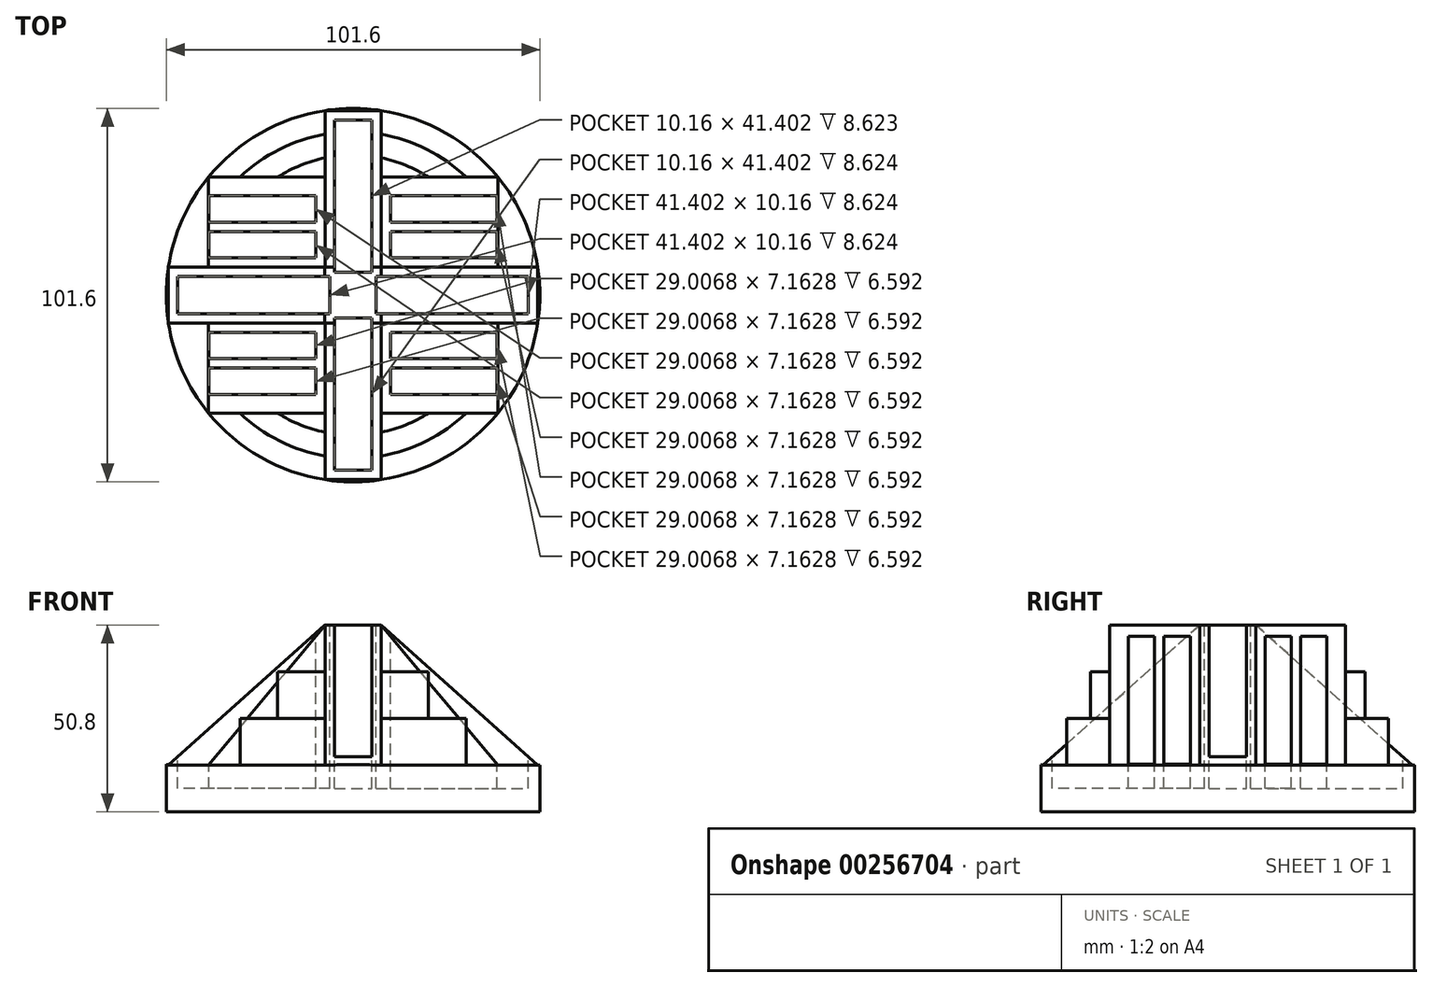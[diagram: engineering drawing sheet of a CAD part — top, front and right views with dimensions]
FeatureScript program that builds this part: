
annotation { "Feature Type Name" : "Feature", "Feature Type Description" : "" }
export const myFeature = defineFeature(function(context is Context, id is Id, definition is map)
    precondition{}
    {
        {
            var Q0;
            Q0=qCreatedBy(makeId("Top.planeOp"),FACE);
            cPlane(context, id + "F0", {"entities" : qUnion([Q0]), "cplaneType" : CPlaneType.OFFSET, "offset" : 50.8 * mm, "width" : 152.4 * mm, "height" : 152.4 * mm});
        }
        {
            var Q0;
            Q0=qCreatedBy(makeId("Top.planeOp"),FACE);
            var sketch = newSketch(context, id + "F1", { "sketchPlane" : qUnion([Q0])});
            skCircle(sketch, "E0", {"center": v(0, 0) * mm, "radius": 50.8 * mm});
            skArc(sketch, "E1", {"start": v(7.62, -43.8) * mm, "mid": v(44.45, 0) * mm, "end": v(7.62, 43.8) * mm});
            skArc(sketch, "E2", {"start": v(7.62, -37.33) * mm, "mid": v(38.1, 0) * mm, "end": v(7.62, 37.33) * mm});
            skCircle(sketch, "E3", {"center": v(0, 0) * mm, "radius": 25.4 * mm});
            skLineSegment(sketch, "E4", {"start": v(-7.62, -24.23) * mm, "end": v(-7.62, -50.23) * mm});
            skLineSegment(sketch, "E5", {"start": v(7.62, -24.23) * mm, "end": v(7.62, -50.23) * mm});
            skLineSegment(sketch, "E6", {"start": v(-7.62, 24.23) * mm, "end": v(-7.62, 50.23) * mm});
            skLineSegment(sketch, "E7", {"start": v(7.62, 24.23) * mm, "end": v(7.62, 50.23) * mm});
            skPoint(sketch, "E8.orphan", {"position": v(0, -25.4) * mm});
            skPoint(sketch, "E9.end.orphan", {"position": v(-3.8, -50.66) * mm});
            skArc(sketch, "E10.trimOffspring", {"start": v(-7.62, 37.33) * mm, "mid": v(-38.1, 0) * mm, "end": v(-7.62, -37.33) * mm});
            skArc(sketch, "E11.trimOffspring", {"start": v(-7.62, 43.8) * mm, "mid": v(-44.45, 0) * mm, "end": v(-7.62, -43.8) * mm});
            skArc(sketch, "E12", {"start": v(-7.62, -43.8) * mm, "mid": v(0, -44.45) * mm, "end": v(7.62, -43.8) * mm});
            skArc(sketch, "E13", {"start": v(-7.62, -37.33) * mm, "mid": v(0, -38.1) * mm, "end": v(7.62, -37.33) * mm});
            skCircle(sketch, "E14", {"center": v(0, 0) * mm, "radius": 31.75 * mm});
            skArc(sketch, "E15.trimOffspring", {"start": v(7.62, 43.8) * mm, "mid": v(0, 44.45) * mm, "end": v(-7.62, 43.8) * mm});
            skArc(sketch, "E16.trimOffspring", {"start": v(7.62, 37.33) * mm, "mid": v(0, 38.1) * mm, "end": v(-7.62, 37.33) * mm});
            skLineSegment(sketch, "E17", {"start": v(-7.62, -24.23) * mm, "end": v(-7.62, 24.23) * mm});
            skLineSegment(sketch, "E18", {"start": v(7.62, 24.23) * mm, "end": v(7.62, -24.23) * mm});
            skLineSegment(sketch, "E19", {"start": v(0, 7.62) * mm, "end": v(-50.23, 7.62) * mm});
            skLineSegment(sketch, "E20", {"start": v(0, 7.62) * mm, "end": v(50.23, 7.62) * mm});
            skLineSegment(sketch, "E21", {"start": v(0, -7.62) * mm, "end": v(50.23, -7.62) * mm});
            skLineSegment(sketch, "E22", {"start": v(0, -7.62) * mm, "end": v(-50.23, -7.62) * mm});
            skLineSegment(sketch, "E23", {"start": v(-17.78, 7.62) * mm, "end": v(7.62, -17.78) * mm});
            skLineSegment(sketch, "E24", {"start": v(-7.62, 17.78) * mm, "end": v(17.78, -7.62) * mm});
            skLineSegment(sketch, "E25", {"start": v(7.62, 17.78) * mm, "end": v(-17.78, -7.62) * mm});
            skLineSegment(sketch, "E26", {"start": v(17.78, 7.62) * mm, "end": v(-7.62, -17.78) * mm});
            skLineSegment(sketch, "E27", {"start": v(-7.62, -19.86) * mm, "end": v(-20.32, -19.86) * mm});
            skLineSegment(sketch, "E28", {"start": v(-20.32, -19.86) * mm, "end": v(-46.76, -19.86) * mm});
            skLineSegment(sketch, "E29.trimOffspring", {"start": v(-20.32, -32.1) * mm, "end": v(-20.32, -32.23) * mm});
            skPoint(sketch, "E30.start.orphan", {"position": v(-20.32, -7.62) * mm});
            skLineSegment(sketch, "E31", {"start": v(-7.62, -32.1) * mm, "end": v(-39.37, -32.1) * mm});
            skLineSegment(sketch, "E32", {"start": v(-7.62, 19.86) * mm, "end": v(-46.76, 19.86) * mm});
            skLineSegment(sketch, "E33", {"start": v(-7.62, 32.1) * mm, "end": v(-39.37, 32.1) * mm});
            skLineSegment(sketch, "E34", {"start": v(7.62, 32.1) * mm, "end": v(39.37, 32.1) * mm});
            skLineSegment(sketch, "E35", {"start": v(7.62, 19.86) * mm, "end": v(46.76, 19.86) * mm});
            skLineSegment(sketch, "E36", {"start": v(7.62, -19.86) * mm, "end": v(46.76, -19.86) * mm});
            skLineSegment(sketch, "E37", {"start": v(7.62, -32.1) * mm, "end": v(39.37, -32.1) * mm});
            skSolve(sketch);
        }
        {
            var Q0;
            {var subQ5=sQuery(id+"F1.wireOp",EDGE,"E11.trimOffspring");Q0=makeQuery(id+"F1.imprint","IMPRINT",FACE,{"disambiguationData":[TD([[makeQuery(id+"F1.imprint","IMPRINT",EDGE,{"derivedFrom":subQ5}),-1.0]])]});}
            var Q1;
            {var subQ5=sQuery(id+"F1.wireOp",EDGE,"E15.trimOffspring");Q1=makeQuery(id+"F1.imprint","IMPRINT",FACE,{"disambiguationData":[TD([[makeQuery(id+"F1.imprint","IMPRINT",EDGE,{"derivedFrom":subQ5}),-1.0]])]});}
            var Q2;
            {var subQ5=sQuery(id+"F1.wireOp",EDGE,"E1");Q2=makeQuery(id+"F1.imprint","IMPRINT",FACE,{"disambiguationData":[TD([[makeQuery(id+"F1.imprint","IMPRINT",EDGE,{"derivedFrom":subQ5}),-1.0]])]});}
            var Q3;
            {var subQ5=sQuery(id+"F1.wireOp",EDGE,"E12");Q3=makeQuery(id+"F1.imprint","IMPRINT",FACE,{"disambiguationData":[TD([[makeQuery(id+"F1.imprint","IMPRINT",EDGE,{"derivedFrom":subQ5}),-1.0]])]});}
            extrude(context, id + "F2", {"entities" : qUnion([Q0, Q1, Q2, Q3]), "depth" : 12.7 * mm});
        }
        {
            var Q0;
            {var subQ0=sQuery(id+"F1.wireOp",EDGE,"E10.trimOffspring");Q0=makeQuery(id+"F1.imprint","IMPRINT",FACE,{"disambiguationData":[TD([[makeQuery(id+"F1.imprint","IMPRINT",EDGE,{"derivedFrom":subQ0}),-1.0]])]});}
            var Q1;
            {var subQ0=sQuery(id+"F1.wireOp",EDGE,"E1");Q1=makeQuery(id+"F1.imprint","IMPRINT",FACE,{"disambiguationData":[TD([[makeQuery(id+"F1.imprint","IMPRINT",EDGE,{"derivedFrom":subQ0}),1.0]])]});}
            var Q2;
            {var subQ2=sQuery(id+"F1.wireOp",EDGE,"E15.trimOffspring");Q2=makeQuery(id+"F1.imprint","IMPRINT",FACE,{"disambiguationData":[TD([[makeQuery(id+"F1.imprint","IMPRINT",EDGE,{"derivedFrom":subQ2}),1.0]])]});}
            var Q3;
            {var subQ2=sQuery(id+"F1.wireOp",EDGE,"E12");Q3=makeQuery(id+"F1.imprint","IMPRINT",FACE,{"disambiguationData":[TD([[makeQuery(id+"F1.imprint","IMPRINT",EDGE,{"derivedFrom":subQ2}),1.0]])]});}
            var Q4;
            {var subQ0=sQuery(id+"F1.wireOp",EDGE,"E10.trimOffspring");var subQ5=sQuery(id+"F1.wireOp",EDGE,"KU0cdiGB-8eOj-Trs3-v5YD-3LzdnCRRimhK");var subQ6=makeQuery(id+"F1.imprint","INTERSECT",VERTEX,{"derivedFrom":[subQ0,subQ5]});Q4=makeQuery(id+"F1.imprint","IMPRINT",FACE,{"disambiguationData":[TD([[makeQuery(id+"F1.imprint","IMPRINT",EDGE,{"disambiguationData":[TD([[subQ6,-1.0]])],"derivedFrom":subQ5}),-1.0]])]});}
            var Q5;
            {var subQ0=sQuery(id+"F1.wireOp",EDGE,"KU0cdiGB-8eOj-Trs3-v5YD-3LzdnCRRimhK");var subQ1=sQuery(id+"F1.wireOp",EDGE,"E10.trimOffspring");var subQ2=makeQuery(id+"F1.imprint","INTERSECT",VERTEX,{"derivedFrom":[subQ1,subQ0]});Q5=makeQuery(id+"F1.imprint","IMPRINT",FACE,{"disambiguationData":[TD([[makeQuery(id+"F1.imprint","IMPRINT",EDGE,{"disambiguationData":[TD([[subQ2,-1.0]])],"derivedFrom":subQ1}),-1.0]])]});}
            var Q6;
            {var subQ0=sQuery(id+"F1.wireOp",EDGE,"n5LII22h-w08l-qE72-yfr9-18N67uZxNTdQ");var subQ1=sQuery(id+"F1.wireOp",EDGE,"E10.trimOffspring");var subQ2=makeQuery(id+"F1.imprint","INTERSECT",VERTEX,{"derivedFrom":[subQ1,subQ0]});Q6=makeQuery(id+"F1.imprint","IMPRINT",FACE,{"disambiguationData":[TD([[makeQuery(id+"F1.imprint","IMPRINT",EDGE,{"disambiguationData":[TD([[subQ2,-1.0]])],"derivedFrom":subQ1}),-1.0]])]});}
            var Q7;
            {var subQ0=sQuery(id+"F1.wireOp",EDGE,"E19");var subQ1=sQuery(id+"F1.wireOp",EDGE,"E10.trimOffspring");var subQ2=makeQuery(id+"F1.imprint","INTERSECT",VERTEX,{"derivedFrom":[subQ1,subQ0]});Q7=makeQuery(id+"F1.imprint","IMPRINT",FACE,{"disambiguationData":[TD([[makeQuery(id+"F1.imprint","IMPRINT",EDGE,{"disambiguationData":[TD([[subQ2,-1.0]])],"derivedFrom":subQ1}),-1.0]])]});}
            var Q8;
            {var subQ0=sQuery(id+"F1.wireOp",EDGE,"E22");var subQ1=sQuery(id+"F1.wireOp",EDGE,"E10.trimOffspring");var subQ2=makeQuery(id+"F1.imprint","INTERSECT",VERTEX,{"derivedFrom":[subQ1,subQ0]});Q8=makeQuery(id+"F1.imprint","IMPRINT",FACE,{"disambiguationData":[TD([[makeQuery(id+"F1.imprint","IMPRINT",EDGE,{"disambiguationData":[TD([[subQ2,-1.0]])],"derivedFrom":subQ1}),-1.0]])]});}
            var Q9;
            {var subQ0=sQuery(id+"F1.wireOp",EDGE,"E28");var subQ1=sQuery(id+"F1.wireOp",EDGE,"E10.trimOffspring");var subQ2=makeQuery(id+"F1.imprint","INTERSECT",VERTEX,{"derivedFrom":[subQ1,subQ0]});Q9=makeQuery(id+"F1.imprint","IMPRINT",FACE,{"disambiguationData":[TD([[makeQuery(id+"F1.imprint","IMPRINT",EDGE,{"disambiguationData":[TD([[subQ2,-1.0]])],"derivedFrom":subQ1}),-1.0]])]});}
            var Q10;
            {var subQ1=sQuery(id+"F1.wireOp",EDGE,"E10.trimOffspring");var subQ5=sQuery(id+"F1.wireOp",EDGE,"E25");var subQ6=makeQuery(id+"F1.imprint","INTERSECT",VERTEX,{"derivedFrom":[subQ1,subQ5]});Q10=makeQuery(id+"F1.imprint","IMPRINT",FACE,{"disambiguationData":[TD([[makeQuery(id+"F1.imprint","IMPRINT",EDGE,{"disambiguationData":[TD([[subQ6,-1.0]])],"derivedFrom":subQ1}),-1.0]])]});}
            var Q11;
            {var subQ0=sQuery(id+"F1.wireOp",EDGE,"E31");var subQ1=sQuery(id+"F1.wireOp",EDGE,"E11.trimOffspring");var subQ2=makeQuery(id+"F1.imprint","INTERSECT",VERTEX,{"derivedFrom":[subQ1,subQ0]});Q11=makeQuery(id+"F1.imprint","IMPRINT",FACE,{"disambiguationData":[TD([[makeQuery(id+"F1.imprint","IMPRINT",EDGE,{"disambiguationData":[TD([[subQ2,-1.0]])],"derivedFrom":subQ1}),1.0]])]});}
            var Q12;
            {var subQ0=sQuery(id+"F1.wireOp",EDGE,"E26");var subQ1=sQuery(id+"F1.wireOp",EDGE,"E10.trimOffspring");var subQ2=makeQuery(id+"F1.imprint","INTERSECT",VERTEX,{"derivedFrom":[subQ1,subQ0]});Q12=makeQuery(id+"F1.imprint","IMPRINT",FACE,{"disambiguationData":[TD([[makeQuery(id+"F1.imprint","IMPRINT",EDGE,{"disambiguationData":[TD([[subQ2,-1.0]])],"derivedFrom":subQ1}),-1.0]])]});}
            var Q13;
            {var subQ0=sQuery(id+"F1.wireOp",EDGE,"E32");var subQ1=sQuery(id+"F1.wireOp",EDGE,"E10.trimOffspring");var subQ2=makeQuery(id+"F1.imprint","INTERSECT",VERTEX,{"derivedFrom":[subQ1,subQ0]});Q13=makeQuery(id+"F1.imprint","IMPRINT",FACE,{"disambiguationData":[TD([[makeQuery(id+"F1.imprint","IMPRINT",EDGE,{"disambiguationData":[TD([[subQ2,-1.0]])],"derivedFrom":subQ1}),-1.0]])]});}
            var Q14;
            {var subQ0=sQuery(id+"F1.wireOp",EDGE,"E33");var subQ1=sQuery(id+"F1.wireOp",EDGE,"E10.trimOffspring");var subQ2=makeQuery(id+"F1.imprint","INTERSECT",VERTEX,{"derivedFrom":[subQ1,subQ0]});Q14=makeQuery(id+"F1.imprint","IMPRINT",FACE,{"disambiguationData":[TD([[makeQuery(id+"F1.imprint","IMPRINT",EDGE,{"disambiguationData":[TD([[subQ2,-1.0]])],"derivedFrom":subQ1}),-1.0]])]});}
            var Q15;
            {var subQ0=sQuery(id+"F1.wireOp",EDGE,"E10.trimOffspring");var subQ5=sQuery(id+"F1.wireOp",EDGE,"E33");var subQ7=makeQuery(id+"F1.imprint","INTERSECT",VERTEX,{"derivedFrom":[subQ0,subQ5]});Q15=makeQuery(id+"F1.imprint","IMPRINT",FACE,{"disambiguationData":[TD([[makeQuery(id+"F1.imprint","IMPRINT",EDGE,{"disambiguationData":[TD([[subQ7,-1.0]])],"derivedFrom":subQ5}),-1.0]])]});}
            extrude(context, id + "F3", {"entities" : qUnion([Q0, Q1, Q2, Q3, Q4, Q5, Q6, Q7, Q8, Q9, Q10, Q11, Q12, Q13, Q14, Q15]), "operationType" : NewBodyOperationType.ADD, "depth" : 25.4 * mm});
        }
        {
            var Q0;
            {var subQ0=sQuery(id+"F1.wireOp",EDGE,"E13");Q0=makeQuery(id+"F1.imprint","IMPRINT",FACE,{"disambiguationData":[TD([[makeQuery(id+"F1.imprint","IMPRINT",EDGE,{"derivedFrom":subQ0}),1.0]])]});}
            var Q1;
            {var subQ0=sQuery(id+"F1.wireOp",EDGE,"E10.trimOffspring");Q1=makeQuery(id+"F1.imprint","IMPRINT",FACE,{"disambiguationData":[TD([[makeQuery(id+"F1.imprint","IMPRINT",EDGE,{"derivedFrom":subQ0}),1.0]])]});}
            var Q2;
            {var subQ0=sQuery(id+"F1.wireOp",EDGE,"E2");Q2=makeQuery(id+"F1.imprint","IMPRINT",FACE,{"disambiguationData":[TD([[makeQuery(id+"F1.imprint","IMPRINT",EDGE,{"derivedFrom":subQ0}),1.0]])]});}
            var Q3;
            {var subQ0=sQuery(id+"F1.wireOp",EDGE,"E16.trimOffspring");Q3=makeQuery(id+"F1.imprint","IMPRINT",FACE,{"disambiguationData":[TD([[makeQuery(id+"F1.imprint","IMPRINT",EDGE,{"derivedFrom":subQ0}),1.0]])]});}
            var Q4;
            {var subQ0=sQuery(id+"F1.wireOp",EDGE,"n5LII22h-w08l-qE72-yfr9-18N67uZxNTdQ");var subQ1=sQuery(id+"F1.wireOp",EDGE,"E10.trimOffspring");var subQ2=makeQuery(id+"F1.imprint","INTERSECT",VERTEX,{"derivedFrom":[subQ1,subQ0]});Q4=makeQuery(id+"F1.imprint","IMPRINT",FACE,{"disambiguationData":[TD([[makeQuery(id+"F1.imprint","IMPRINT",EDGE,{"disambiguationData":[TD([[subQ2,-1.0]])],"derivedFrom":subQ1}),1.0]])]});}
            var Q5;
            {var subQ0=sQuery(id+"F1.wireOp",EDGE,"KU0cdiGB-8eOj-Trs3-v5YD-3LzdnCRRimhK");var subQ1=sQuery(id+"F1.wireOp",EDGE,"E10.trimOffspring");var subQ2=makeQuery(id+"F1.imprint","INTERSECT",VERTEX,{"derivedFrom":[subQ1,subQ0]});Q5=makeQuery(id+"F1.imprint","IMPRINT",FACE,{"disambiguationData":[TD([[makeQuery(id+"F1.imprint","IMPRINT",EDGE,{"disambiguationData":[TD([[subQ2,-1.0]])],"derivedFrom":subQ1}),1.0]])]});}
            var Q6;
            {var subQ1=sQuery(id+"F1.wireOp",EDGE,"E6");var subQ3=sQuery(id+"F1.wireOp",EDGE,"E14");var subQ4=makeQuery(id+"F1.imprint","INTERSECT",VERTEX,{"derivedFrom":[subQ1,subQ3]});Q6=makeQuery(id+"F1.imprint","IMPRINT",FACE,{"disambiguationData":[TD([[makeQuery(id+"F1.imprint","IMPRINT",EDGE,{"disambiguationData":[TD([[subQ4,-1.0]])],"derivedFrom":subQ3}),-1.0]])]});}
            var Q7;
            {var subQ0=sQuery(id+"F1.wireOp",EDGE,"E7");var subQ5=sQuery(id+"F1.wireOp",EDGE,"E14");var subQ6=makeQuery(id+"F1.imprint","INTERSECT",VERTEX,{"derivedFrom":[subQ0,subQ5]});Q7=makeQuery(id+"F1.imprint","IMPRINT",FACE,{"disambiguationData":[TD([[makeQuery(id+"F1.imprint","IMPRINT",EDGE,{"disambiguationData":[TD([[subQ6,1.0]])],"derivedFrom":subQ5}),-1.0]])]});}
            var Q8;
            {var subQ0=sQuery(id+"F1.wireOp",EDGE,"E19");var subQ1=sQuery(id+"F1.wireOp",EDGE,"E10.trimOffspring");var subQ2=makeQuery(id+"F1.imprint","INTERSECT",VERTEX,{"derivedFrom":[subQ1,subQ0]});Q8=makeQuery(id+"F1.imprint","IMPRINT",FACE,{"disambiguationData":[TD([[makeQuery(id+"F1.imprint","IMPRINT",EDGE,{"disambiguationData":[TD([[subQ2,-1.0]])],"derivedFrom":subQ1}),1.0]])]});}
            var Q9;
            {var subQ0=sQuery(id+"F1.wireOp",EDGE,"E22");var subQ1=sQuery(id+"F1.wireOp",EDGE,"E10.trimOffspring");var subQ2=makeQuery(id+"F1.imprint","INTERSECT",VERTEX,{"derivedFrom":[subQ1,subQ0]});Q9=makeQuery(id+"F1.imprint","IMPRINT",FACE,{"disambiguationData":[TD([[makeQuery(id+"F1.imprint","IMPRINT",EDGE,{"disambiguationData":[TD([[subQ2,-1.0]])],"derivedFrom":subQ1}),1.0]])]});}
            var Q10;
            {var subQ0=sQuery(id+"F1.wireOp",EDGE,"E25");var subQ1=sQuery(id+"F1.wireOp",EDGE,"E10.trimOffspring");var subQ2=makeQuery(id+"F1.imprint","INTERSECT",VERTEX,{"derivedFrom":[subQ1,subQ0]});Q10=makeQuery(id+"F1.imprint","IMPRINT",FACE,{"disambiguationData":[TD([[makeQuery(id+"F1.imprint","IMPRINT",EDGE,{"disambiguationData":[TD([[subQ2,-1.0]])],"derivedFrom":subQ1}),1.0]])]});}
            var Q11;
            {var subQ3=sQuery(id+"F1.wireOp",EDGE,"E14");var subQ7=sQuery(id+"F1.wireOp",EDGE,"E4");var subQ8=makeQuery(id+"F1.imprint","INTERSECT",VERTEX,{"derivedFrom":[subQ7,subQ3]});Q11=makeQuery(id+"F1.imprint","IMPRINT",FACE,{"disambiguationData":[TD([[makeQuery(id+"F1.imprint","IMPRINT",EDGE,{"disambiguationData":[TD([[subQ8,-1.0]])],"derivedFrom":subQ7}),-1.0]])]});}
            var Q12;
            {var subQ1=sQuery(id+"F1.wireOp",EDGE,"E2");var subQ5=sQuery(id+"F1.wireOp",EDGE,"dChad7VG-r3lr-Y0ra-zuCQ-UW0r8UzcO7aT");var subQ6=makeQuery(id+"F1.imprint","INTERSECT",VERTEX,{"derivedFrom":[subQ1,subQ5]});Q12=makeQuery(id+"F1.imprint","IMPRINT",FACE,{"disambiguationData":[TD([[makeQuery(id+"F1.imprint","IMPRINT",EDGE,{"disambiguationData":[TD([[subQ6,-1.0]])],"derivedFrom":subQ1}),1.0]])]});}
            var Q13;
            {var subQ0=sQuery(id+"F1.wireOp",EDGE,"E23");var subQ1=sQuery(id+"F1.wireOp",EDGE,"E2");var subQ2=makeQuery(id+"F1.imprint","INTERSECT",VERTEX,{"derivedFrom":[subQ1,subQ0]});Q13=makeQuery(id+"F1.imprint","IMPRINT",FACE,{"disambiguationData":[TD([[makeQuery(id+"F1.imprint","IMPRINT",EDGE,{"disambiguationData":[TD([[subQ2,-1.0]])],"derivedFrom":subQ1}),1.0]])]});}
            var Q14;
            {var subQ0=sQuery(id+"F1.wireOp",EDGE,"E24");var subQ1=sQuery(id+"F1.wireOp",EDGE,"E2");var subQ2=makeQuery(id+"F1.imprint","INTERSECT",VERTEX,{"derivedFrom":[subQ1,subQ0]});Q14=makeQuery(id+"F1.imprint","IMPRINT",FACE,{"disambiguationData":[TD([[makeQuery(id+"F1.imprint","IMPRINT",EDGE,{"disambiguationData":[TD([[subQ2,-1.0]])],"derivedFrom":subQ1}),1.0]])]});}
            var Q15;
            {var subQ0=sQuery(id+"F1.wireOp",EDGE,"E21");var subQ1=sQuery(id+"F1.wireOp",EDGE,"E2");var subQ2=makeQuery(id+"F1.imprint","INTERSECT",VERTEX,{"derivedFrom":[subQ1,subQ0]});Q15=makeQuery(id+"F1.imprint","IMPRINT",FACE,{"disambiguationData":[TD([[makeQuery(id+"F1.imprint","IMPRINT",EDGE,{"disambiguationData":[TD([[subQ2,-1.0]])],"derivedFrom":subQ1}),1.0]])]});}
            var Q16;
            {var subQ0=sQuery(id+"F1.wireOp",EDGE,"E20");var subQ1=sQuery(id+"F1.wireOp",EDGE,"E2");var subQ2=makeQuery(id+"F1.imprint","INTERSECT",VERTEX,{"derivedFrom":[subQ1,subQ0]});Q16=makeQuery(id+"F1.imprint","IMPRINT",FACE,{"disambiguationData":[TD([[makeQuery(id+"F1.imprint","IMPRINT",EDGE,{"disambiguationData":[TD([[subQ2,-1.0]])],"derivedFrom":subQ1}),1.0]])]});}
            var Q17;
            {var subQ0=sQuery(id+"F1.wireOp",EDGE,"SVIod6WE-LFFt-Ms97-owyS-8ShU65W6W8it");var subQ1=sQuery(id+"F1.wireOp",EDGE,"E2");var subQ2=makeQuery(id+"F1.imprint","INTERSECT",VERTEX,{"derivedFrom":[subQ1,subQ0]});Q17=makeQuery(id+"F1.imprint","IMPRINT",FACE,{"disambiguationData":[TD([[makeQuery(id+"F1.imprint","IMPRINT",EDGE,{"disambiguationData":[TD([[subQ2,-1.0]])],"derivedFrom":subQ1}),1.0]])]});}
            var Q18;
            {var subQ0=sQuery(id+"F1.wireOp",EDGE,"E25");var subQ1=sQuery(id+"F1.wireOp",EDGE,"E14");var subQ2=makeQuery(id+"F1.imprint","INTERSECT",VERTEX,{"derivedFrom":[subQ1,subQ0]});Q18=makeQuery(id+"F1.imprint","IMPRINT",FACE,{"disambiguationData":[TD([[makeQuery(id+"F1.imprint","IMPRINT",EDGE,{"disambiguationData":[TD([[subQ2,-1.0]])],"derivedFrom":subQ1}),-1.0]])]});}
            var Q19;
            {var subQ0=sQuery(id+"F1.wireOp",EDGE,"E30");var subQ1=sQuery(id+"F1.wireOp",EDGE,"E14");var subQ2=makeQuery(id+"F1.imprint","INTERSECT",VERTEX,{"derivedFrom":[subQ1,subQ0]});Q19=makeQuery(id+"F1.imprint","IMPRINT",FACE,{"disambiguationData":[TD([[makeQuery(id+"F1.imprint","IMPRINT",EDGE,{"disambiguationData":[TD([[subQ2,-1.0]])],"derivedFrom":subQ1}),-1.0]])]});}
            var Q20;
            {var subQ5=sQuery(id+"F1.wireOp",EDGE,"E29.trimOffspring");Q20=makeQuery(id+"F1.imprint","IMPRINT",FACE,{"disambiguationData":[TD([[makeQuery(id+"F1.imprint","IMPRINT",EDGE,{"derivedFrom":subQ5}),1.0]])]});}
            var Q21;
            {var subQ1=sQuery(id+"F1.wireOp",EDGE,"E2");var subQ7=sQuery(id+"F1.wireOp",EDGE,"E37");var subQ9=makeQuery(id+"F1.imprint","INTERSECT",VERTEX,{"derivedFrom":[subQ1,subQ7]});Q21=makeQuery(id+"F1.imprint","IMPRINT",FACE,{"disambiguationData":[TD([[makeQuery(id+"F1.imprint","IMPRINT",EDGE,{"disambiguationData":[TD([[subQ9,-1.0]])],"derivedFrom":subQ1}),1.0]])]});}
            extrude(context, id + "F4", {"entities" : qUnion([Q0, Q1, Q2, Q3, Q4, Q5, Q6, Q7, Q8, Q9, Q10, Q11, Q12, Q13, Q14, Q15, Q16, Q17, Q18, Q19, Q20, Q21]), "operationType" : NewBodyOperationType.ADD, "depth" : 38.1 * mm});
        }
        {
            var Q0;
            {var subQ0=sQuery(id+"F1.wireOp",EDGE,"E6");var subQ1=sQuery(id+"F1.wireOp",EDGE,"E3");var subQ2=makeQuery(id+"F1.imprint","INTERSECT",VERTEX,{"derivedFrom":[subQ1,subQ0]});Q0=makeQuery(id+"F1.imprint","IMPRINT",FACE,{"disambiguationData":[TD([[makeQuery(id+"F1.imprint","IMPRINT",EDGE,{"disambiguationData":[TD([[subQ2,1.0]])],"derivedFrom":subQ1}),-1.0]])]});}
            var Q1;
            {var subQ0=sQuery(id+"F1.wireOp",EDGE,"E4");var subQ1=sQuery(id+"F1.wireOp",EDGE,"E3");var subQ2=makeQuery(id+"F1.imprint","INTERSECT",VERTEX,{"derivedFrom":[subQ1,subQ0]});Q1=makeQuery(id+"F1.imprint","IMPRINT",FACE,{"disambiguationData":[TD([[makeQuery(id+"F1.imprint","IMPRINT",EDGE,{"disambiguationData":[TD([[subQ2,-1.0]])],"derivedFrom":subQ1}),-1.0]])]});}
            var Q2;
            {var subQ0=sQuery(id+"F1.wireOp",EDGE,"E5");var subQ1=sQuery(id+"F1.wireOp",EDGE,"E3");var subQ2=makeQuery(id+"F1.imprint","INTERSECT",VERTEX,{"derivedFrom":[subQ1,subQ0]});Q2=makeQuery(id+"F1.imprint","IMPRINT",FACE,{"disambiguationData":[TD([[makeQuery(id+"F1.imprint","IMPRINT",EDGE,{"disambiguationData":[TD([[subQ2,-1.0]])],"derivedFrom":subQ1}),-1.0]])]});}
            var Q3;
            {var subQ0=sQuery(id+"F1.wireOp",EDGE,"E7");var subQ5=sQuery(id+"F1.wireOp",EDGE,"E14");var subQ6=makeQuery(id+"F1.imprint","INTERSECT",VERTEX,{"derivedFrom":[subQ0,subQ5]});Q3=makeQuery(id+"F1.imprint","IMPRINT",FACE,{"disambiguationData":[TD([[makeQuery(id+"F1.imprint","IMPRINT",EDGE,{"disambiguationData":[TD([[subQ6,1.0]])],"derivedFrom":subQ5}),1.0]])]});}
            var Q4;
            {var subQ0=sQuery(id+"F1.wireOp",EDGE,"E19");var subQ1=sQuery(id+"F1.wireOp",EDGE,"E3");var subQ2=makeQuery(id+"F1.imprint","INTERSECT",VERTEX,{"derivedFrom":[subQ1,subQ0]});Q4=makeQuery(id+"F1.imprint","IMPRINT",FACE,{"disambiguationData":[TD([[makeQuery(id+"F1.imprint","IMPRINT",EDGE,{"disambiguationData":[TD([[subQ2,-1.0]])],"derivedFrom":subQ1}),-1.0]])]});}
            var Q5;
            {var subQ0=sQuery(id+"F1.wireOp",EDGE,"E6");var subQ5=sQuery(id+"F1.wireOp",EDGE,"E14");var subQ6=makeQuery(id+"F1.imprint","INTERSECT",VERTEX,{"derivedFrom":[subQ0,subQ5]});Q5=makeQuery(id+"F1.imprint","IMPRINT",FACE,{"disambiguationData":[TD([[makeQuery(id+"F1.imprint","IMPRINT",EDGE,{"disambiguationData":[TD([[subQ6,-1.0]])],"derivedFrom":subQ5}),1.0]])]});}
            var Q6;
            {var subQ0=sQuery(id+"F1.wireOp",EDGE,"E20");var subQ1=sQuery(id+"F1.wireOp",EDGE,"E3");var subQ2=makeQuery(id+"F1.imprint","INTERSECT",VERTEX,{"derivedFrom":[subQ1,subQ0]});Q6=makeQuery(id+"F1.imprint","IMPRINT",FACE,{"disambiguationData":[TD([[makeQuery(id+"F1.imprint","IMPRINT",EDGE,{"disambiguationData":[TD([[subQ2,1.0]])],"derivedFrom":subQ1}),-1.0]])]});}
            var Q7;
            {var subQ1=sQuery(id+"F1.wireOp",EDGE,"E4");var subQ3=sQuery(id+"F1.wireOp",EDGE,"E14");var subQ4=makeQuery(id+"F1.imprint","INTERSECT",VERTEX,{"derivedFrom":[subQ1,subQ3]});Q7=makeQuery(id+"F1.imprint","IMPRINT",FACE,{"disambiguationData":[TD([[makeQuery(id+"F1.imprint","IMPRINT",EDGE,{"disambiguationData":[TD([[subQ4,1.0]])],"derivedFrom":subQ3}),1.0]])]});}
            var Q8;
            {var subQ3=sQuery(id+"F1.wireOp",EDGE,"6cIBHAnO-3Gdr-gs2R-q8mb-qejxkHO2rhEE");var subQ5=sQuery(id+"F1.wireOp",EDGE,"E14");var subQ6=makeQuery(id+"F1.imprint","INTERSECT",VERTEX,{"derivedFrom":[subQ5,subQ3]});Q8=makeQuery(id+"F1.imprint","IMPRINT",FACE,{"disambiguationData":[TD([[makeQuery(id+"F1.imprint","IMPRINT",EDGE,{"disambiguationData":[TD([[subQ6,-1.0]])],"derivedFrom":subQ5}),1.0]])]});}
            var Q9;
            {var subQ0=sQuery(id+"F1.wireOp",EDGE,"E22");var subQ1=sQuery(id+"F1.wireOp",EDGE,"E14");var subQ2=makeQuery(id+"F1.imprint","INTERSECT",VERTEX,{"derivedFrom":[subQ1,subQ0]});Q9=makeQuery(id+"F1.imprint","IMPRINT",FACE,{"disambiguationData":[TD([[makeQuery(id+"F1.imprint","IMPRINT",EDGE,{"disambiguationData":[TD([[subQ2,-1.0]])],"derivedFrom":subQ1}),1.0]])]});}
            var Q10;
            {var subQ3=sQuery(id+"F1.wireOp",EDGE,"1679b663-5bbc-411f-b373-dbe6ce103e45.trimOffspring");var subQ5=sQuery(id+"F1.wireOp",EDGE,"E14");var subQ7=makeQuery(id+"F1.imprint","INTERSECT",VERTEX,{"disambiguationData":[OD(1.0)],"derivedFrom":[subQ5,subQ3]});Q10=makeQuery(id+"F1.imprint","IMPRINT",FACE,{"disambiguationData":[TD([[makeQuery(id+"F1.imprint","IMPRINT",EDGE,{"disambiguationData":[TD([[subQ7,-1.0]])],"derivedFrom":subQ5}),1.0]])]});}
            var Q11;
            {var subQ3=sQuery(id+"F1.wireOp",EDGE,"8l5Dcz2D-qY2G-ceuh-glFK-kLwJx8DI5XpU");var subQ5=sQuery(id+"F1.wireOp",EDGE,"E14");var subQ7=makeQuery(id+"F1.imprint","INTERSECT",VERTEX,{"derivedFrom":[subQ5,subQ3]});Q11=makeQuery(id+"F1.imprint","IMPRINT",FACE,{"disambiguationData":[TD([[makeQuery(id+"F1.imprint","IMPRINT",EDGE,{"disambiguationData":[TD([[subQ7,-1.0]])],"derivedFrom":subQ5}),1.0]])]});}
            var Q12;
            {var subQ0=sQuery(id+"F1.wireOp",EDGE,"n5LII22h-w08l-qE72-yfr9-18N67uZxNTdQ");var subQ1=sQuery(id+"F1.wireOp",EDGE,"E3");var subQ2=makeQuery(id+"F1.imprint","INTERSECT",VERTEX,{"derivedFrom":[subQ1,subQ0]});Q12=makeQuery(id+"F1.imprint","IMPRINT",FACE,{"disambiguationData":[TD([[makeQuery(id+"F1.imprint","IMPRINT",EDGE,{"disambiguationData":[TD([[subQ2,-1.0]])],"derivedFrom":subQ1}),-1.0]])]});}
            var Q13;
            {var subQ0=sQuery(id+"F1.wireOp",EDGE,"KU0cdiGB-8eOj-Trs3-v5YD-3LzdnCRRimhK");var subQ1=sQuery(id+"F1.wireOp",EDGE,"E3");var subQ2=makeQuery(id+"F1.imprint","INTERSECT",VERTEX,{"derivedFrom":[subQ1,subQ0]});Q13=makeQuery(id+"F1.imprint","IMPRINT",FACE,{"disambiguationData":[TD([[makeQuery(id+"F1.imprint","IMPRINT",EDGE,{"disambiguationData":[TD([[subQ2,-1.0]])],"derivedFrom":subQ1}),-1.0]])]});}
            var Q14;
            {var subQ0=sQuery(id+"F1.wireOp",EDGE,"SVIod6WE-LFFt-Ms97-owyS-8ShU65W6W8it");var subQ1=sQuery(id+"F1.wireOp",EDGE,"E3");var subQ2=makeQuery(id+"F1.imprint","INTERSECT",VERTEX,{"derivedFrom":[subQ1,subQ0]});Q14=makeQuery(id+"F1.imprint","IMPRINT",FACE,{"disambiguationData":[TD([[makeQuery(id+"F1.imprint","IMPRINT",EDGE,{"disambiguationData":[TD([[subQ2,-1.0]])],"derivedFrom":subQ1}),-1.0]])]});}
            var Q15;
            {var subQ0=sQuery(id+"F1.wireOp",EDGE,"SVIod6WE-LFFt-Ms97-owyS-8ShU65W6W8it");var subQ1=sQuery(id+"F1.wireOp",EDGE,"E3");var subQ2=makeQuery(id+"F1.imprint","INTERSECT",VERTEX,{"derivedFrom":[subQ1,subQ0]});Q15=makeQuery(id+"F1.imprint","IMPRINT",FACE,{"disambiguationData":[TD([[makeQuery(id+"F1.imprint","IMPRINT",EDGE,{"disambiguationData":[TD([[subQ2,1.0]])],"derivedFrom":subQ1}),-1.0]])]});}
            var Q16;
            {var subQ0=sQuery(id+"F1.wireOp",EDGE,"E24");var subQ1=sQuery(id+"F1.wireOp",EDGE,"E3");var subQ2=makeQuery(id+"F1.imprint","INTERSECT",VERTEX,{"derivedFrom":[subQ1,subQ0]});Q16=makeQuery(id+"F1.imprint","IMPRINT",FACE,{"disambiguationData":[TD([[makeQuery(id+"F1.imprint","IMPRINT",EDGE,{"disambiguationData":[TD([[subQ2,-1.0]])],"derivedFrom":subQ1}),-1.0]])]});}
            var Q17;
            {var subQ0=sQuery(id+"F1.wireOp",EDGE,"E23");var subQ1=sQuery(id+"F1.wireOp",EDGE,"E3");var subQ2=makeQuery(id+"F1.imprint","INTERSECT",VERTEX,{"derivedFrom":[subQ1,subQ0]});Q17=makeQuery(id+"F1.imprint","IMPRINT",FACE,{"disambiguationData":[TD([[makeQuery(id+"F1.imprint","IMPRINT",EDGE,{"disambiguationData":[TD([[subQ2,-1.0]])],"derivedFrom":subQ1}),-1.0]])]});}
            var Q18;
            {var subQ1=sQuery(id+"F1.wireOp",EDGE,"E27");var subQ3=sQuery(id+"F1.wireOp",EDGE,"E3");var subQ4=makeQuery(id+"F1.imprint","INTERSECT",VERTEX,{"derivedFrom":[subQ3,subQ1]});Q18=makeQuery(id+"F1.imprint","IMPRINT",FACE,{"disambiguationData":[TD([[makeQuery(id+"F1.imprint","IMPRINT",EDGE,{"disambiguationData":[TD([[subQ4,-1.0]])],"derivedFrom":subQ3}),-1.0]])]});}
            var Q19;
            {var subQ0=sQuery(id+"F1.wireOp",EDGE,"E30");var subQ1=sQuery(id+"F1.wireOp",EDGE,"E3");var subQ2=makeQuery(id+"F1.imprint","INTERSECT",VERTEX,{"derivedFrom":[subQ1,subQ0]});Q19=makeQuery(id+"F1.imprint","IMPRINT",FACE,{"disambiguationData":[TD([[makeQuery(id+"F1.imprint","IMPRINT",EDGE,{"disambiguationData":[TD([[subQ2,-1.0]])],"derivedFrom":subQ1}),-1.0]])]});}
            var Q20;
            {var subQ0=sQuery(id+"F1.wireOp",EDGE,"E25");var subQ7=sQuery(id+"F1.wireOp",EDGE,"E3");var subQ8=makeQuery(id+"F1.imprint","INTERSECT",VERTEX,{"derivedFrom":[subQ7,subQ0]});Q20=makeQuery(id+"F1.imprint","IMPRINT",FACE,{"disambiguationData":[TD([[makeQuery(id+"F1.imprint","IMPRINT",EDGE,{"disambiguationData":[TD([[subQ8,-1.0]])],"derivedFrom":subQ7}),-1.0]])]});}
            extrude(context, id + "F5", {"entities" : qUnion([Q0, Q1, Q2, Q3, Q4, Q5, Q6, Q7, Q8, Q9, Q10, Q11, Q12, Q13, Q14, Q15, Q16, Q17, Q18, Q19, Q20]), "operationType" : NewBodyOperationType.ADD, "depth" : 50.8 * mm});
        }
        {
            var Q0;
            {var subQ5=sQuery(id+"F1.wireOp",EDGE,"E12");Q0=makeQuery(id+"F1.imprint","IMPRINT",FACE,{"disambiguationData":[TD([[makeQuery(id+"F1.imprint","IMPRINT",EDGE,{"derivedFrom":subQ5}),-1.0]])]});}
            var Q1;
            {var subQ0=sQuery(id+"F1.wireOp",EDGE,"E13");Q1=makeQuery(id+"F1.imprint","IMPRINT",FACE,{"disambiguationData":[TD([[makeQuery(id+"F1.imprint","IMPRINT",EDGE,{"derivedFrom":subQ0}),1.0]])]});}
            var Q2;
            {var subQ0=sQuery(id+"F1.wireOp",EDGE,"E4");var subQ1=sQuery(id+"F1.wireOp",EDGE,"E3");var subQ2=makeQuery(id+"F1.imprint","INTERSECT",VERTEX,{"derivedFrom":[subQ1,subQ0]});Q2=makeQuery(id+"F1.imprint","IMPRINT",FACE,{"disambiguationData":[TD([[makeQuery(id+"F1.imprint","IMPRINT",EDGE,{"disambiguationData":[TD([[subQ2,-1.0]])],"derivedFrom":subQ1}),-1.0]])]});}
            var Q3;
            {var subQ2=sQuery(id+"F1.wireOp",EDGE,"E12");Q3=makeQuery(id+"F1.imprint","IMPRINT",FACE,{"disambiguationData":[TD([[makeQuery(id+"F1.imprint","IMPRINT",EDGE,{"derivedFrom":subQ2}),1.0]])]});}
            var Q4;
            {var subQ0=sQuery(id+"F1.wireOp",EDGE,"E17");Q4=makeQuery(id+"F1.imprint","IMPRINT",FACE,{"disambiguationData":[TD([[makeQuery(id+"F1.imprint","IMPRINT",EDGE,{"derivedFrom":subQ0}),-1.0]])]});}
            var Q5;
            {var subQ0=sQuery(id+"F1.wireOp",EDGE,"E6");var subQ5=sQuery(id+"F1.wireOp",EDGE,"E14");var subQ6=makeQuery(id+"F1.imprint","INTERSECT",VERTEX,{"derivedFrom":[subQ0,subQ5]});Q5=makeQuery(id+"F1.imprint","IMPRINT",FACE,{"disambiguationData":[TD([[makeQuery(id+"F1.imprint","IMPRINT",EDGE,{"disambiguationData":[TD([[subQ6,1.0]])],"derivedFrom":subQ5}),1.0]])]});}
            var Q6;
            {var subQ0=sQuery(id+"F1.wireOp",EDGE,"E16.trimOffspring");Q6=makeQuery(id+"F1.imprint","IMPRINT",FACE,{"disambiguationData":[TD([[makeQuery(id+"F1.imprint","IMPRINT",EDGE,{"derivedFrom":subQ0}),1.0]])]});}
            var Q7;
            {var subQ2=sQuery(id+"F1.wireOp",EDGE,"E15.trimOffspring");Q7=makeQuery(id+"F1.imprint","IMPRINT",FACE,{"disambiguationData":[TD([[makeQuery(id+"F1.imprint","IMPRINT",EDGE,{"derivedFrom":subQ2}),1.0]])]});}
            var Q8;
            {var subQ5=sQuery(id+"F1.wireOp",EDGE,"E15.trimOffspring");Q8=makeQuery(id+"F1.imprint","IMPRINT",FACE,{"disambiguationData":[TD([[makeQuery(id+"F1.imprint","IMPRINT",EDGE,{"derivedFrom":subQ5}),-1.0]])]});}
            var Q9;
            {var subQ0=sQuery(id+"F1.wireOp",EDGE,"8l5Dcz2D-qY2G-ceuh-glFK-kLwJx8DI5XpU");var subQ3=sQuery(id+"F1.wireOp",EDGE,"E18");var subQ5=makeQuery(id+"F1.imprint","INTERSECT",VERTEX,{"derivedFrom":[subQ3,subQ0]});Q9=makeQuery(id+"F1.imprint","IMPRINT",FACE,{"disambiguationData":[TD([[makeQuery(id+"F1.imprint","IMPRINT",EDGE,{"disambiguationData":[TD([[subQ5,-1.0]])],"derivedFrom":subQ3}),-1.0]])]});}
            var Q10;
            {var subQ1=sQuery(id+"F1.wireOp",EDGE,"E21");var subQ5=sQuery(id+"F1.wireOp",EDGE,"E18");var subQ6=makeQuery(id+"F1.imprint","INTERSECT",VERTEX,{"derivedFrom":[subQ5,subQ1]});Q10=makeQuery(id+"F1.imprint","IMPRINT",FACE,{"disambiguationData":[TD([[makeQuery(id+"F1.imprint","IMPRINT",EDGE,{"disambiguationData":[TD([[subQ6,-1.0]])],"derivedFrom":subQ5}),-1.0]])]});}
            var Q11;
            {var subQ1=sQuery(id+"F1.wireOp",EDGE,"E19");var subQ7=sQuery(id+"F1.wireOp",EDGE,"E17");var subQ8=makeQuery(id+"F1.imprint","INTERSECT",VERTEX,{"derivedFrom":[subQ7,subQ1]});Q11=makeQuery(id+"F1.imprint","IMPRINT",FACE,{"disambiguationData":[TD([[makeQuery(id+"F1.imprint","IMPRINT",EDGE,{"disambiguationData":[TD([[subQ8,-1.0]])],"derivedFrom":subQ7}),-1.0]])]});}
            var Q12;
            {var subQ3=sQuery(id+"F1.wireOp",EDGE,"E17");var subQ9=sQuery(id+"F1.wireOp",EDGE,"E22");var subQ10=makeQuery(id+"F1.imprint","INTERSECT",VERTEX,{"derivedFrom":[subQ3,subQ9]});Q12=makeQuery(id+"F1.imprint","IMPRINT",FACE,{"disambiguationData":[TD([[makeQuery(id+"F1.imprint","IMPRINT",EDGE,{"disambiguationData":[TD([[subQ10,-1.0]])],"derivedFrom":subQ3}),-1.0]])]});}
            var Q13;
            {var subQ0=sQuery(id+"F1.wireOp",EDGE,"E22");var subQ1=sQuery(id+"F1.wireOp",EDGE,"E17");var subQ2=makeQuery(id+"F1.imprint","INTERSECT",VERTEX,{"derivedFrom":[subQ1,subQ0]});Q13=makeQuery(id+"F1.imprint","IMPRINT",FACE,{"disambiguationData":[TD([[makeQuery(id+"F1.imprint","IMPRINT",EDGE,{"disambiguationData":[TD([[subQ2,1.0]])],"derivedFrom":subQ0}),1.0]])]});}
            var Q14;
            {var subQ3=sQuery(id+"F1.wireOp",EDGE,"E17");var subQ11=sQuery(id+"F1.wireOp",EDGE,"E23");var subQ12=makeQuery(id+"F1.imprint","INTERSECT",VERTEX,{"derivedFrom":[subQ3,subQ11]});Q14=makeQuery(id+"F1.imprint","IMPRINT",FACE,{"disambiguationData":[TD([[makeQuery(id+"F1.imprint","IMPRINT",EDGE,{"disambiguationData":[TD([[subQ12,-1.0]])],"derivedFrom":subQ3}),-1.0]])]});}
            var Q15;
            {var subQ0=sQuery(id+"F1.wireOp",EDGE,"E20");var subQ1=sQuery(id+"F1.wireOp",EDGE,"E18");var subQ2=makeQuery(id+"F1.imprint","INTERSECT",VERTEX,{"derivedFrom":[subQ1,subQ0]});Q15=makeQuery(id+"F1.imprint","IMPRINT",FACE,{"disambiguationData":[TD([[makeQuery(id+"F1.imprint","IMPRINT",EDGE,{"disambiguationData":[TD([[subQ2,1.0]])],"derivedFrom":subQ0}),1.0]])]});}
            var Q16;
            {var subQ0=sQuery(id+"F1.wireOp",EDGE,"E18");var subQ3=sQuery(id+"F1.wireOp",EDGE,"E23");var subQ4=makeQuery(id+"F1.imprint","INTERSECT",VERTEX,{"derivedFrom":[subQ0,subQ3]});Q16=makeQuery(id+"F1.imprint","IMPRINT",FACE,{"disambiguationData":[TD([[makeQuery(id+"F1.imprint","IMPRINT",EDGE,{"disambiguationData":[TD([[subQ4,1.0]])],"derivedFrom":subQ3}),-1.0]])]});}
            var Q17;
            {var subQ0=sQuery(id+"F1.wireOp",EDGE,"E24");var subQ3=sQuery(id+"F1.wireOp",EDGE,"E25");var subQ4=makeQuery(id+"F1.imprint","INTERSECT",VERTEX,{"derivedFrom":[subQ0,subQ3]});Q17=makeQuery(id+"F1.imprint","IMPRINT",FACE,{"disambiguationData":[TD([[makeQuery(id+"F1.imprint","IMPRINT",EDGE,{"disambiguationData":[TD([[subQ4,1.0]])],"derivedFrom":subQ0}),1.0]])]});}
            var Q18;
            {var subQ0=sQuery(id+"F1.wireOp",EDGE,"E20");var subQ1=sQuery(id+"F1.wireOp",EDGE,"E19");var subQ2=makeQuery(id+"F1.imprint","INTERSECT",VERTEX,{"derivedFrom":[subQ1,subQ0]});Q18=makeQuery(id+"F1.imprint","IMPRINT",FACE,{"disambiguationData":[TD([[makeQuery(id+"F1.imprint","IMPRINT",EDGE,{"disambiguationData":[TD([[subQ2,-1.0]])],"derivedFrom":subQ1}),-1.0]])]});}
            var Q19;
            {var subQ0=sQuery(id+"F1.wireOp",EDGE,"E22");var subQ1=sQuery(id+"F1.wireOp",EDGE,"E21");var subQ2=makeQuery(id+"F1.imprint","INTERSECT",VERTEX,{"derivedFrom":[subQ1,subQ0]});Q19=makeQuery(id+"F1.imprint","IMPRINT",FACE,{"disambiguationData":[TD([[makeQuery(id+"F1.imprint","IMPRINT",EDGE,{"disambiguationData":[TD([[subQ2,-1.0]])],"derivedFrom":subQ1}),-1.0]])]});}
            var Q20;
            {var subQ0=sQuery(id+"F1.wireOp",EDGE,"E25");var subQ1=sQuery(id+"F1.wireOp",EDGE,"E17");var subQ2=makeQuery(id+"F1.imprint","INTERSECT",VERTEX,{"derivedFrom":[subQ1,subQ0]});Q20=makeQuery(id+"F1.imprint","IMPRINT",FACE,{"disambiguationData":[TD([[makeQuery(id+"F1.imprint","IMPRINT",EDGE,{"disambiguationData":[TD([[subQ2,-1.0]])],"derivedFrom":subQ1}),-1.0]])]});}
            var Q21;
            {var subQ0=sQuery(id+"F1.wireOp",EDGE,"E26");var subQ1=sQuery(id+"F1.wireOp",EDGE,"E18");var subQ2=makeQuery(id+"F1.imprint","INTERSECT",VERTEX,{"derivedFrom":[subQ1,subQ0]});Q21=makeQuery(id+"F1.imprint","IMPRINT",FACE,{"disambiguationData":[TD([[makeQuery(id+"F1.imprint","IMPRINT",EDGE,{"disambiguationData":[TD([[subQ2,-1.0]])],"derivedFrom":subQ1}),-1.0]])]});}
            var Q22;
            {var subQ0=sQuery(id+"F1.wireOp",EDGE,"E20");var subQ1=sQuery(id+"F1.wireOp",EDGE,"E18");var subQ2=makeQuery(id+"F1.imprint","INTERSECT",VERTEX,{"derivedFrom":[subQ1,subQ0]});Q22=makeQuery(id+"F1.imprint","IMPRINT",FACE,{"disambiguationData":[TD([[makeQuery(id+"F1.imprint","IMPRINT",EDGE,{"disambiguationData":[TD([[subQ2,-1.0]])],"derivedFrom":subQ1}),-1.0]])]});}
            extrude(context, id + "F6", {"entities" : qUnion([Q0, Q1, Q2, Q3, Q4, Q5, Q6, Q7, Q8, Q9, Q10, Q11, Q12, Q13, Q14, Q15, Q16, Q17, Q18, Q19, Q20, Q21, Q22]), "operationType" : NewBodyOperationType.ADD, "depth" : 50.8 * mm});
        }
        {
            var Q0;
            {var subQ0=sQuery(id+"F1.wireOp",EDGE,"SVIod6WE-LFFt-Ms97-owyS-8ShU65W6W8it");var subQ1=sQuery(id+"F1.wireOp",EDGE,"E3");var subQ2=makeQuery(id+"F1.imprint","INTERSECT",VERTEX,{"derivedFrom":[subQ1,subQ0]});Q0=makeQuery(id+"F1.imprint","IMPRINT",FACE,{"disambiguationData":[TD([[makeQuery(id+"F1.imprint","IMPRINT",EDGE,{"disambiguationData":[TD([[subQ2,1.0]])],"derivedFrom":subQ1}),1.0]])]});}
            var Q1;
            {var subQ1=sQuery(id+"F1.wireOp",EDGE,"E3");var subQ3=sQuery(id+"F1.wireOp",EDGE,"I2xWRYXB-6D2N-iSpQ-MyaY-Cu2MAQN8JGNk");var subQ4=makeQuery(id+"F1.imprint","INTERSECT",VERTEX,{"derivedFrom":[subQ1,subQ3]});Q1=makeQuery(id+"F1.imprint","IMPRINT",FACE,{"disambiguationData":[TD([[makeQuery(id+"F1.imprint","IMPRINT",EDGE,{"disambiguationData":[TD([[subQ4,-1.0]])],"derivedFrom":subQ1}),1.0]])]});}
            var Q2;
            {var subQ0=sQuery(id+"F1.wireOp",EDGE,"n5LII22h-w08l-qE72-yfr9-18N67uZxNTdQ");var subQ1=sQuery(id+"F1.wireOp",EDGE,"E3");var subQ2=makeQuery(id+"F1.imprint","INTERSECT",VERTEX,{"derivedFrom":[subQ1,subQ0]});Q2=makeQuery(id+"F1.imprint","IMPRINT",FACE,{"disambiguationData":[TD([[makeQuery(id+"F1.imprint","IMPRINT",EDGE,{"disambiguationData":[TD([[subQ2,-1.0]])],"derivedFrom":subQ1}),1.0]])]});}
            var Q3;
            {var subQ0=sQuery(id+"F1.wireOp",EDGE,"E22");var subQ1=sQuery(id+"F1.wireOp",EDGE,"E3");var subQ2=makeQuery(id+"F1.imprint","INTERSECT",VERTEX,{"derivedFrom":[subQ1,subQ0]});Q3=makeQuery(id+"F1.imprint","IMPRINT",FACE,{"disambiguationData":[TD([[makeQuery(id+"F1.imprint","IMPRINT",EDGE,{"disambiguationData":[TD([[subQ2,-1.0]])],"derivedFrom":subQ1}),1.0]])]});}
            var Q4;
            {var subQ0=sQuery(id+"F1.wireOp",EDGE,"E27");var subQ1=sQuery(id+"F1.wireOp",EDGE,"E3");var subQ2=makeQuery(id+"F1.imprint","INTERSECT",VERTEX,{"derivedFrom":[subQ1,subQ0]});Q4=makeQuery(id+"F1.imprint","IMPRINT",FACE,{"disambiguationData":[TD([[makeQuery(id+"F1.imprint","IMPRINT",EDGE,{"disambiguationData":[TD([[subQ2,-1.0]])],"derivedFrom":subQ1}),1.0]])]});}
            var Q5;
            {var subQ0=sQuery(id+"F1.wireOp",EDGE,"E19");var subQ1=sQuery(id+"F1.wireOp",EDGE,"E0");var subQ2=makeQuery(id+"F1.imprint","INTERSECT",VERTEX,{"derivedFrom":[subQ1,subQ0]});Q5=makeQuery(id+"F1.imprint","IMPRINT",FACE,{"disambiguationData":[TD([[makeQuery(id+"F1.imprint","IMPRINT",EDGE,{"disambiguationData":[TD([[subQ2,-1.0]])],"derivedFrom":subQ1}),1.0]])]});}
            var Q6;
            {var subQ0=sQuery(id+"F1.wireOp",EDGE,"E19");var subQ1=sQuery(id+"F1.wireOp",EDGE,"E10.trimOffspring");var subQ2=makeQuery(id+"F1.imprint","INTERSECT",VERTEX,{"derivedFrom":[subQ1,subQ0]});Q6=makeQuery(id+"F1.imprint","IMPRINT",FACE,{"disambiguationData":[TD([[makeQuery(id+"F1.imprint","IMPRINT",EDGE,{"disambiguationData":[TD([[subQ2,-1.0]])],"derivedFrom":subQ1}),-1.0]])]});}
            var Q7;
            {var subQ0=sQuery(id+"F1.wireOp",EDGE,"E19");var subQ1=sQuery(id+"F1.wireOp",EDGE,"E10.trimOffspring");var subQ2=makeQuery(id+"F1.imprint","INTERSECT",VERTEX,{"derivedFrom":[subQ1,subQ0]});Q7=makeQuery(id+"F1.imprint","IMPRINT",FACE,{"disambiguationData":[TD([[makeQuery(id+"F1.imprint","IMPRINT",EDGE,{"disambiguationData":[TD([[subQ2,-1.0]])],"derivedFrom":subQ1}),1.0]])]});}
            var Q8;
            {var subQ0=sQuery(id+"F1.wireOp",EDGE,"E19");var subQ1=sQuery(id+"F1.wireOp",EDGE,"E3");var subQ2=makeQuery(id+"F1.imprint","INTERSECT",VERTEX,{"derivedFrom":[subQ1,subQ0]});Q8=makeQuery(id+"F1.imprint","IMPRINT",FACE,{"disambiguationData":[TD([[makeQuery(id+"F1.imprint","IMPRINT",EDGE,{"disambiguationData":[TD([[subQ2,-1.0]])],"derivedFrom":subQ1}),-1.0]])]});}
            var Q9;
            {var subQ1=sQuery(id+"F1.wireOp",EDGE,"E19");var subQ6=sQuery(id+"F1.wireOp",EDGE,"E3");var subQ9=makeQuery(id+"F1.imprint","INTERSECT",VERTEX,{"derivedFrom":[subQ6,subQ1]});Q9=makeQuery(id+"F1.imprint","IMPRINT",FACE,{"disambiguationData":[TD([[makeQuery(id+"F1.imprint","IMPRINT",EDGE,{"disambiguationData":[TD([[subQ9,-1.0]])],"derivedFrom":subQ6}),1.0]])]});}
            var Q10;
            {var subQ0=sQuery(id+"F1.wireOp",EDGE,"E22");var subQ1=sQuery(id+"F1.wireOp",EDGE,"E17");var subQ2=makeQuery(id+"F1.imprint","INTERSECT",VERTEX,{"derivedFrom":[subQ1,subQ0]});Q10=makeQuery(id+"F1.imprint","IMPRINT",FACE,{"disambiguationData":[TD([[makeQuery(id+"F1.imprint","IMPRINT",EDGE,{"disambiguationData":[TD([[subQ2,-1.0]])],"derivedFrom":subQ1}),-1.0]])]});}
            var Q11;
            {var subQ1=sQuery(id+"F1.wireOp",EDGE,"E3");var subQ7=sQuery(id+"F1.wireOp",EDGE,"E20");var subQ9=makeQuery(id+"F1.imprint","INTERSECT",VERTEX,{"derivedFrom":[subQ1,subQ7]});Q11=makeQuery(id+"F1.imprint","IMPRINT",FACE,{"disambiguationData":[TD([[makeQuery(id+"F1.imprint","IMPRINT",EDGE,{"disambiguationData":[TD([[subQ9,1.0]])],"derivedFrom":subQ1}),1.0]])]});}
            var Q12;
            {var subQ0=sQuery(id+"F1.wireOp",EDGE,"E20");var subQ1=sQuery(id+"F1.wireOp",EDGE,"E3");var subQ2=makeQuery(id+"F1.imprint","INTERSECT",VERTEX,{"derivedFrom":[subQ1,subQ0]});Q12=makeQuery(id+"F1.imprint","IMPRINT",FACE,{"disambiguationData":[TD([[makeQuery(id+"F1.imprint","IMPRINT",EDGE,{"disambiguationData":[TD([[subQ2,1.0]])],"derivedFrom":subQ1}),-1.0]])]});}
            var Q13;
            {var subQ0=sQuery(id+"F1.wireOp",EDGE,"E21");var subQ1=sQuery(id+"F1.wireOp",EDGE,"E2");var subQ2=makeQuery(id+"F1.imprint","INTERSECT",VERTEX,{"derivedFrom":[subQ1,subQ0]});Q13=makeQuery(id+"F1.imprint","IMPRINT",FACE,{"disambiguationData":[TD([[makeQuery(id+"F1.imprint","IMPRINT",EDGE,{"disambiguationData":[TD([[subQ2,-1.0]])],"derivedFrom":subQ1}),1.0]])]});}
            var Q14;
            {var subQ0=sQuery(id+"F1.wireOp",EDGE,"E21");var subQ1=sQuery(id+"F1.wireOp",EDGE,"E1");var subQ2=makeQuery(id+"F1.imprint","INTERSECT",VERTEX,{"derivedFrom":[subQ1,subQ0]});Q14=makeQuery(id+"F1.imprint","IMPRINT",FACE,{"disambiguationData":[TD([[makeQuery(id+"F1.imprint","IMPRINT",EDGE,{"disambiguationData":[TD([[subQ2,-1.0]])],"derivedFrom":subQ1}),1.0]])]});}
            var Q15;
            {var subQ0=sQuery(id+"F1.wireOp",EDGE,"E20");var subQ1=sQuery(id+"F1.wireOp",EDGE,"E0");var subQ2=makeQuery(id+"F1.imprint","INTERSECT",VERTEX,{"derivedFrom":[subQ1,subQ0]});Q15=makeQuery(id+"F1.imprint","IMPRINT",FACE,{"disambiguationData":[TD([[makeQuery(id+"F1.imprint","IMPRINT",EDGE,{"disambiguationData":[TD([[subQ2,1.0]])],"derivedFrom":subQ1}),1.0]])]});}
            var Q16;
            {var subQ0=sQuery(id+"F1.wireOp",EDGE,"E22");var subQ1=sQuery(id+"F1.wireOp",EDGE,"E17");var subQ2=makeQuery(id+"F1.imprint","INTERSECT",VERTEX,{"derivedFrom":[subQ1,subQ0]});Q16=makeQuery(id+"F1.imprint","IMPRINT",FACE,{"disambiguationData":[TD([[makeQuery(id+"F1.imprint","IMPRINT",EDGE,{"disambiguationData":[TD([[subQ2,-1.0]])],"derivedFrom":subQ1}),1.0]])]});}
            var Q17;
            {var subQ0=sQuery(id+"F1.wireOp",EDGE,"E20");var subQ1=sQuery(id+"F1.wireOp",EDGE,"E18");var subQ2=makeQuery(id+"F1.imprint","INTERSECT",VERTEX,{"derivedFrom":[subQ1,subQ0]});Q17=makeQuery(id+"F1.imprint","IMPRINT",FACE,{"disambiguationData":[TD([[makeQuery(id+"F1.imprint","IMPRINT",EDGE,{"disambiguationData":[TD([[subQ2,-1.0]])],"derivedFrom":subQ1}),1.0]])]});}
            var Q18;
            {var subQ0=sQuery(id+"F1.wireOp",EDGE,"E23");var subQ1=sQuery(id+"F1.wireOp",EDGE,"E17");var subQ2=makeQuery(id+"F1.imprint","INTERSECT",VERTEX,{"derivedFrom":[subQ1,subQ0]});Q18=makeQuery(id+"F1.imprint","IMPRINT",FACE,{"disambiguationData":[TD([[makeQuery(id+"F1.imprint","IMPRINT",EDGE,{"disambiguationData":[TD([[subQ2,-1.0]])],"derivedFrom":subQ1}),1.0]])]});}
            var Q19;
            {var subQ0=sQuery(id+"F1.wireOp",EDGE,"E24");var subQ1=sQuery(id+"F1.wireOp",EDGE,"E18");var subQ2=makeQuery(id+"F1.imprint","INTERSECT",VERTEX,{"derivedFrom":[subQ1,subQ0]});Q19=makeQuery(id+"F1.imprint","IMPRINT",FACE,{"disambiguationData":[TD([[makeQuery(id+"F1.imprint","IMPRINT",EDGE,{"disambiguationData":[TD([[subQ2,-1.0]])],"derivedFrom":subQ1}),1.0]])]});}
            var Q20;
            {var subQ0=sQuery(id+"F1.wireOp",EDGE,"KU0cdiGB-8eOj-Trs3-v5YD-3LzdnCRRimhK");var subQ3=sQuery(id+"F1.wireOp",EDGE,"E3");var subQ4=makeQuery(id+"F1.imprint","INTERSECT",VERTEX,{"derivedFrom":[subQ3,subQ0]});Q20=makeQuery(id+"F1.imprint","IMPRINT",FACE,{"disambiguationData":[TD([[makeQuery(id+"F1.imprint","IMPRINT",EDGE,{"disambiguationData":[TD([[subQ4,-1.0]])],"derivedFrom":subQ3}),1.0]])]});}
            var Q21;
            {var subQ0=sQuery(id+"F1.wireOp",EDGE,"E25");var subQ1=sQuery(id+"F1.wireOp",EDGE,"E17");var subQ2=makeQuery(id+"F1.imprint","INTERSECT",VERTEX,{"derivedFrom":[subQ1,subQ0]});Q21=makeQuery(id+"F1.imprint","IMPRINT",FACE,{"disambiguationData":[TD([[makeQuery(id+"F1.imprint","IMPRINT",EDGE,{"disambiguationData":[TD([[subQ2,-1.0]])],"derivedFrom":subQ1}),1.0]])]});}
            var Q22;
            {var subQ0=sQuery(id+"F1.wireOp",EDGE,"E26");var subQ1=sQuery(id+"F1.wireOp",EDGE,"E18");var subQ2=makeQuery(id+"F1.imprint","INTERSECT",VERTEX,{"derivedFrom":[subQ1,subQ0]});Q22=makeQuery(id+"F1.imprint","IMPRINT",FACE,{"disambiguationData":[TD([[makeQuery(id+"F1.imprint","IMPRINT",EDGE,{"disambiguationData":[TD([[subQ2,-1.0]])],"derivedFrom":subQ1}),1.0]])]});}
            var Q23;
            {var subQ3=sQuery(id+"F1.wireOp",EDGE,"E25");var subQ5=sQuery(id+"F1.wireOp",EDGE,"E3");var subQ6=makeQuery(id+"F1.imprint","INTERSECT",VERTEX,{"derivedFrom":[subQ5,subQ3]});Q23=makeQuery(id+"F1.imprint","IMPRINT",FACE,{"disambiguationData":[TD([[makeQuery(id+"F1.imprint","IMPRINT",EDGE,{"disambiguationData":[TD([[subQ6,-1.0]])],"derivedFrom":subQ5}),1.0]])]});}
            var Q24;
            {var subQ0=sQuery(id+"F1.wireOp",EDGE,"E27");var subQ1=sQuery(id+"F1.wireOp",EDGE,"E3");var subQ2=makeQuery(id+"F1.imprint","INTERSECT",VERTEX,{"derivedFrom":[subQ1,subQ0]});Q24=makeQuery(id+"F1.imprint","IMPRINT",FACE,{"disambiguationData":[TD([[makeQuery(id+"F1.imprint","IMPRINT",EDGE,{"disambiguationData":[TD([[subQ2,-1.0]])],"derivedFrom":subQ1}),1.0]])]});}
            var Q25;
            {var subQ0=sQuery(id+"F1.wireOp",EDGE,"SVIod6WE-LFFt-Ms97-owyS-8ShU65W6W8it");var subQ7=sQuery(id+"F1.wireOp",EDGE,"E3");var subQ9=makeQuery(id+"F1.imprint","INTERSECT",VERTEX,{"derivedFrom":[subQ7,subQ0]});Q25=makeQuery(id+"F1.imprint","IMPRINT",FACE,{"disambiguationData":[TD([[makeQuery(id+"F1.imprint","IMPRINT",EDGE,{"disambiguationData":[TD([[subQ9,-1.0]])],"derivedFrom":subQ7}),1.0]])]});}
            var Q26;
            {var subQ0=sQuery(id+"F1.wireOp",EDGE,"E24");var subQ1=sQuery(id+"F1.wireOp",EDGE,"E3");var subQ2=makeQuery(id+"F1.imprint","INTERSECT",VERTEX,{"derivedFrom":[subQ1,subQ0]});Q26=makeQuery(id+"F1.imprint","IMPRINT",FACE,{"disambiguationData":[TD([[makeQuery(id+"F1.imprint","IMPRINT",EDGE,{"disambiguationData":[TD([[subQ2,-1.0]])],"derivedFrom":subQ1}),1.0]])]});}
            var Q27;
            {var subQ0=sQuery(id+"F1.wireOp",EDGE,"E23");var subQ1=sQuery(id+"F1.wireOp",EDGE,"E3");var subQ2=makeQuery(id+"F1.imprint","INTERSECT",VERTEX,{"derivedFrom":[subQ1,subQ0]});Q27=makeQuery(id+"F1.imprint","IMPRINT",FACE,{"disambiguationData":[TD([[makeQuery(id+"F1.imprint","IMPRINT",EDGE,{"disambiguationData":[TD([[subQ2,-1.0]])],"derivedFrom":subQ1}),1.0]])]});}
            var Q28;
            {var subQ1=sQuery(id+"F1.wireOp",EDGE,"E3");var subQ3=sQuery(id+"F1.wireOp",EDGE,"E23");var subQ4=makeQuery(id+"F1.imprint","INTERSECT",VERTEX,{"derivedFrom":[subQ1,subQ3]});Q28=makeQuery(id+"F1.imprint","IMPRINT",FACE,{"disambiguationData":[TD([[makeQuery(id+"F1.imprint","IMPRINT",EDGE,{"disambiguationData":[TD([[subQ4,1.0]])],"derivedFrom":subQ3}),-1.0]])]});}
            var Q29;
            {var subQ1=sQuery(id+"F1.wireOp",EDGE,"E3");var subQ3=sQuery(id+"F1.wireOp",EDGE,"E26");var subQ4=makeQuery(id+"F1.imprint","INTERSECT",VERTEX,{"derivedFrom":[subQ1,subQ3]});Q29=makeQuery(id+"F1.imprint","IMPRINT",FACE,{"disambiguationData":[TD([[makeQuery(id+"F1.imprint","IMPRINT",EDGE,{"disambiguationData":[TD([[subQ4,1.0]])],"derivedFrom":subQ3}),1.0]])]});}
            var Q30;
            {var subQ1=sQuery(id+"F1.wireOp",EDGE,"E3");var subQ3=sQuery(id+"F1.wireOp",EDGE,"KU0cdiGB-8eOj-Trs3-v5YD-3LzdnCRRimhK");var subQ4=makeQuery(id+"F1.imprint","INTERSECT",VERTEX,{"derivedFrom":[subQ1,subQ3]});Q30=makeQuery(id+"F1.imprint","IMPRINT",FACE,{"disambiguationData":[TD([[makeQuery(id+"F1.imprint","IMPRINT",EDGE,{"disambiguationData":[TD([[subQ4,1.0]])],"derivedFrom":subQ1}),1.0]])]});}
            var Q31;
            {var subQ0=sQuery(id+"F1.wireOp",EDGE,"E27");var subQ1=sQuery(id+"F1.wireOp",EDGE,"E17");var subQ2=makeQuery(id+"F1.imprint","INTERSECT",VERTEX,{"derivedFrom":[subQ1,subQ0]});Q31=makeQuery(id+"F1.imprint","IMPRINT",FACE,{"disambiguationData":[TD([[makeQuery(id+"F1.imprint","IMPRINT",EDGE,{"disambiguationData":[TD([[subQ2,-1.0]])],"derivedFrom":subQ1}),1.0]])]});}
            var Q32;
            {var subQ5=sQuery(id+"F1.wireOp",EDGE,"E36");var subQ7=sQuery(id+"F1.wireOp",EDGE,"E3");var subQ9=makeQuery(id+"F1.imprint","INTERSECT",VERTEX,{"derivedFrom":[subQ7,subQ5]});Q32=makeQuery(id+"F1.imprint","IMPRINT",FACE,{"disambiguationData":[TD([[makeQuery(id+"F1.imprint","IMPRINT",EDGE,{"disambiguationData":[TD([[subQ9,-1.0]])],"derivedFrom":subQ7}),1.0]])]});}
            var Q33;
            {var subQ5=sQuery(id+"F1.wireOp",EDGE,"E35");var subQ7=sQuery(id+"F1.wireOp",EDGE,"E3");var subQ8=makeQuery(id+"F1.imprint","INTERSECT",VERTEX,{"derivedFrom":[subQ7,subQ5]});Q33=makeQuery(id+"F1.imprint","IMPRINT",FACE,{"disambiguationData":[TD([[makeQuery(id+"F1.imprint","IMPRINT",EDGE,{"disambiguationData":[TD([[subQ8,1.0]])],"derivedFrom":subQ7}),1.0]])]});}
            var Q34;
            {var subQ5=sQuery(id+"F1.wireOp",EDGE,"E32");var subQ7=sQuery(id+"F1.wireOp",EDGE,"E3");var subQ8=makeQuery(id+"F1.imprint","INTERSECT",VERTEX,{"derivedFrom":[subQ7,subQ5]});Q34=makeQuery(id+"F1.imprint","IMPRINT",FACE,{"disambiguationData":[TD([[makeQuery(id+"F1.imprint","IMPRINT",EDGE,{"disambiguationData":[TD([[subQ8,-1.0]])],"derivedFrom":subQ7}),1.0]])]});}
            extrude(context, id + "F7", {"entities" : qUnion([Q0, Q1, Q2, Q3, Q4, Q5, Q6, Q7, Q8, Q9, Q10, Q11, Q12, Q13, Q14, Q15, Q16, Q17, Q18, Q19, Q20, Q21, Q22, Q23, Q24, Q25, Q26, Q27, Q28, Q29, Q30, Q31, Q32, Q33, Q34]), "operationType" : NewBodyOperationType.ADD, "depth" : 50.8 * mm});
        }
        {
            var Q0;
            {var subQ0=sQuery(id+"F1.wireOp",EDGE,"E20");var subQ1=sQuery(id+"F1.wireOp",EDGE,"E19");var subQ2=sQuery(id+"F1.wireOp",EDGE,"E18");var subQ3=sQuery(id+"F1.wireOp",EDGE,"E17");var subQ4=sQuery(id+"F1.wireOp",EDGE,"E7");var subQ5=sQuery(id+"F1.wireOp",EDGE,"E6");var subQ6=sQuery(id+"F1.wireOp",EDGE,"E0");var subQ7=sQuery(id+"F1.wireOp",EDGE,"E14");var subQ8=sQuery(id+"F1.wireOp",EDGE,"E15.trimOffspring");var subQ9=sQuery(id+"F1.wireOp",EDGE,"E12");var subQ10=sQuery(id+"F1.wireOp",EDGE,"E11.trimOffspring");var subQ11=sQuery(id+"F1.wireOp",EDGE,"E1");var subQ12=sQuery(id+"F1.wireOp",EDGE,"E16.trimOffspring");var subQ13=sQuery(id+"F1.wireOp",EDGE,"E13");var subQ14=sQuery(id+"F1.wireOp",EDGE,"E10.trimOffspring");var subQ15=sQuery(id+"F1.wireOp",EDGE,"E2");var subQ16=sQuery(id+"F1.wireOp",EDGE,"E4");var subQ17=sQuery(id+"F1.wireOp",EDGE,"E5");var subQ18=sQuery(id+"F1.wireOp",EDGE,"E22");var subQ19=sQuery(id+"F1.wireOp",EDGE,"E21");Q0=makeQuery(id+"F7.boolean.opBoolean","SPLIT",FACE,{"disambiguationData":[TD([makeQuery(id+"F2.opExtrude","SWEPT_FACE",FACE,{"disambiguationData":[OSD([subQ6])]}),makeQuery(id+"F2.opExtrude","CAP_FACE",FACE,{"disambiguationData":[OSD([subQ6,subQ11,subQ10,subQ9,subQ8])],"isStart":false}),makeQuery(id+"F3.opExtrude","CAP_FACE",FACE,{"disambiguationData":[OSD([subQ11,subQ15,subQ14,subQ10,subQ9,subQ13,subQ8,subQ12])],"isStart":false}),makeQuery(id+"F3.opExtrude","SWEPT_FACE",FACE,{"disambiguationData":[OSD([subQ11,subQ10,subQ9,subQ8])]}),makeQuery(id+"F4.opExtrude","CAP_FACE",FACE,{"disambiguationData":[OSD([subQ15,subQ14,subQ13,subQ7,subQ12])],"isStart":false}),makeQuery(id+"F4.opExtrude","SWEPT_FACE",FACE,{"disambiguationData":[OSD([subQ15,subQ14,subQ13,subQ12])]}),makeQuery(id+"F5.opExtrude","CAP_FACE",FACE,{"disambiguationData":[OSD([sQuery(id+"F1.wireOp",EDGE,"E3"),subQ7])],"isStart":false}),makeQuery(id+"F5.opExtrude","SWEPT_FACE",FACE,{"disambiguationData":[OSD([subQ7])]}),makeQuery(id+"F6.opExtrude","SWEPT_FACE",FACE,{"disambiguationData":[OSD([subQ6]),TDD([makeQuery(id+"F1.imprint","IMPRINT",EDGE,{"disambiguationData":[TD([[makeQuery(id+"F1.imprint","INTERSECT",VERTEX,{"derivedFrom":[subQ6,subQ5]}),1.0]])],"derivedFrom":subQ6})])]}),makeQuery(id+"F6.opExtrude","CAP_FACE",FACE,{"disambiguationData":[OSD([subQ6,subQ5,subQ4,subQ3,subQ2,subQ1,subQ0])],"isStart":false}),makeQuery(id+"F6.opExtrude","SWEPT_FACE",FACE,{"disambiguationData":[OSD([subQ6]),TDD([makeQuery(id+"F1.imprint","IMPRINT",EDGE,{"disambiguationData":[TD([[makeQuery(id+"F1.imprint","INTERSECT",VERTEX,{"derivedFrom":[subQ6,subQ16]}),-1.0]])],"derivedFrom":subQ6})])]}),makeQuery(id+"F6.opExtrude","CAP_FACE",FACE,{"disambiguationData":[OSD([subQ6,subQ16,subQ17,subQ3,subQ2,subQ19,subQ18])],"isStart":false}),makeQuery(id+"F7.opExtrude","SWEPT_FACE",FACE,{"disambiguationData":[OSD([subQ6]),TDD([makeQuery(id+"F1.imprint","IMPRINT",EDGE,{"disambiguationData":[TD([[makeQuery(id+"F1.imprint","INTERSECT",VERTEX,{"derivedFrom":[subQ6,subQ1]}),-1.0]])],"derivedFrom":subQ6})])]}),makeQuery(id+"F7.opExtrude","CAP_FACE",FACE,{"disambiguationData":[OSD([subQ6,subQ1,subQ0,subQ19,subQ18])],"isStart":false}),makeQuery(id+"F7.opExtrude","SWEPT_FACE",FACE,{"disambiguationData":[OSD([subQ6]),TDD([makeQuery(id+"F1.imprint","IMPRINT",EDGE,{"disambiguationData":[TD([[makeQuery(id+"F1.imprint","INTERSECT",VERTEX,{"derivedFrom":[subQ6,subQ0]}),1.0]])],"derivedFrom":subQ6})])]})]),OD(1.0)],"derivedFrom":makeQuery(id+"F7.opExtrude","SWEPT_FACE",FACE,{"disambiguationData":[OSD([subQ19,subQ18])]})});}
            var sketch = newSketch(context, id + "F8", { "sketchPlane" : qUnion([Q0])});
            skLineSegment(sketch, "E38", {"start": v(-50.23, 12.7) * mm, "end": v(-7.66, 50.8) * mm});
            skLineSegment(sketch, "E39", {"start": v(-7.66, 50.8) * mm, "end": v(-7.66, 64.83) * mm});
            skLineSegment(sketch, "E40", {"start": v(-7.66, 64.83) * mm, "end": v(-55.92, 64.83) * mm});
            skLineSegment(sketch, "E41", {"start": v(-55.92, 64.83) * mm, "end": v(-54.33, 14.23) * mm});
            skLineSegment(sketch, "E42", {"start": v(-54.33, 14.23) * mm, "end": v(-50.23, 12.7) * mm});
            skSolve(sketch);
        }
        {
            var Q0;
            {var subQ0=sQuery(id+"F1.wireOp",EDGE,"E20");var subQ1=sQuery(id+"F1.wireOp",EDGE,"E19");var subQ2=sQuery(id+"F1.wireOp",EDGE,"E18");var subQ3=sQuery(id+"F1.wireOp",EDGE,"E17");var subQ4=sQuery(id+"F1.wireOp",EDGE,"E7");var subQ5=sQuery(id+"F1.wireOp",EDGE,"E6");var subQ6=sQuery(id+"F1.wireOp",EDGE,"E0");var subQ7=sQuery(id+"F1.wireOp",EDGE,"E14");var subQ8=sQuery(id+"F1.wireOp",EDGE,"E15.trimOffspring");var subQ9=sQuery(id+"F1.wireOp",EDGE,"E12");var subQ10=sQuery(id+"F1.wireOp",EDGE,"E11.trimOffspring");var subQ11=sQuery(id+"F1.wireOp",EDGE,"E1");var subQ12=sQuery(id+"F1.wireOp",EDGE,"E16.trimOffspring");var subQ13=sQuery(id+"F1.wireOp",EDGE,"E13");var subQ14=sQuery(id+"F1.wireOp",EDGE,"E10.trimOffspring");var subQ15=sQuery(id+"F1.wireOp",EDGE,"E2");var subQ16=sQuery(id+"F1.wireOp",EDGE,"E4");var subQ17=sQuery(id+"F1.wireOp",EDGE,"E5");var subQ18=sQuery(id+"F1.wireOp",EDGE,"E22");var subQ19=sQuery(id+"F1.wireOp",EDGE,"E21");Q0=makeQuery(id+"F7.boolean.opBoolean","SPLIT",FACE,{"disambiguationData":[TD([makeQuery(id+"F2.opExtrude","SWEPT_FACE",FACE,{"disambiguationData":[OSD([subQ6])]}),makeQuery(id+"F2.opExtrude","CAP_FACE",FACE,{"disambiguationData":[OSD([subQ6,subQ11,subQ10,subQ9,subQ8])],"isStart":false}),makeQuery(id+"F3.opExtrude","CAP_FACE",FACE,{"disambiguationData":[OSD([subQ11,subQ15,subQ14,subQ10,subQ9,subQ13,subQ8,subQ12])],"isStart":false}),makeQuery(id+"F3.opExtrude","SWEPT_FACE",FACE,{"disambiguationData":[OSD([subQ11,subQ10,subQ9,subQ8])]}),makeQuery(id+"F4.opExtrude","CAP_FACE",FACE,{"disambiguationData":[OSD([subQ15,subQ14,subQ13,subQ7,subQ12])],"isStart":false}),makeQuery(id+"F4.opExtrude","SWEPT_FACE",FACE,{"disambiguationData":[OSD([subQ15,subQ14,subQ13,subQ12])]}),makeQuery(id+"F5.opExtrude","CAP_FACE",FACE,{"disambiguationData":[OSD([sQuery(id+"F1.wireOp",EDGE,"E3"),subQ7])],"isStart":false}),makeQuery(id+"F5.opExtrude","SWEPT_FACE",FACE,{"disambiguationData":[OSD([subQ7])]}),makeQuery(id+"F6.opExtrude","SWEPT_FACE",FACE,{"disambiguationData":[OSD([subQ6]),TDD([makeQuery(id+"F1.imprint","IMPRINT",EDGE,{"disambiguationData":[TD([[makeQuery(id+"F1.imprint","INTERSECT",VERTEX,{"derivedFrom":[subQ6,subQ5]}),1.0]])],"derivedFrom":subQ6})])]}),makeQuery(id+"F6.opExtrude","CAP_FACE",FACE,{"disambiguationData":[OSD([subQ6,subQ5,subQ4,subQ3,subQ2,subQ1,subQ0])],"isStart":false}),makeQuery(id+"F6.opExtrude","SWEPT_FACE",FACE,{"disambiguationData":[OSD([subQ6]),TDD([makeQuery(id+"F1.imprint","IMPRINT",EDGE,{"disambiguationData":[TD([[makeQuery(id+"F1.imprint","INTERSECT",VERTEX,{"derivedFrom":[subQ6,subQ16]}),-1.0]])],"derivedFrom":subQ6})])]}),makeQuery(id+"F6.opExtrude","CAP_FACE",FACE,{"disambiguationData":[OSD([subQ6,subQ16,subQ17,subQ3,subQ2,subQ19,subQ18])],"isStart":false}),makeQuery(id+"F7.opExtrude","SWEPT_FACE",FACE,{"disambiguationData":[OSD([subQ6]),TDD([makeQuery(id+"F1.imprint","IMPRINT",EDGE,{"disambiguationData":[TD([[makeQuery(id+"F1.imprint","INTERSECT",VERTEX,{"derivedFrom":[subQ6,subQ1]}),-1.0]])],"derivedFrom":subQ6})])]}),makeQuery(id+"F7.opExtrude","CAP_FACE",FACE,{"disambiguationData":[OSD([subQ6,subQ1,subQ0,subQ19,subQ18])],"isStart":false}),makeQuery(id+"F7.opExtrude","SWEPT_FACE",FACE,{"disambiguationData":[OSD([subQ6]),TDD([makeQuery(id+"F1.imprint","IMPRINT",EDGE,{"disambiguationData":[TD([[makeQuery(id+"F1.imprint","INTERSECT",VERTEX,{"derivedFrom":[subQ6,subQ0]}),1.0]])],"derivedFrom":subQ6})])]})]),OD(0.0)],"derivedFrom":makeQuery(id+"F7.opExtrude","SWEPT_FACE",FACE,{"disambiguationData":[OSD([subQ19,subQ18])]})});}
            var sketch = newSketch(context, id + "F9", { "sketchPlane" : qUnion([Q0])});
            skLineSegment(sketch, "E43", {"start": v(50.23, 12.7) * mm, "end": v(7.67, 50.8) * mm});
            skLineSegment(sketch, "E44", {"start": v(7.67, 50.8) * mm, "end": v(7.67, 53.93) * mm});
            skLineSegment(sketch, "E45", {"start": v(7.67, 53.93) * mm, "end": v(55.4, 55.84) * mm});
            skLineSegment(sketch, "E46", {"start": v(55.4, 55.84) * mm, "end": v(55.4, 12.7) * mm});
            skLineSegment(sketch, "E47", {"start": v(55.4, 12.7) * mm, "end": v(50.23, 12.7) * mm});
            skSolve(sketch);
        }
        {
            var Q0;
            {var subQ0=sQuery(id+"F1.wireOp",EDGE,"E18");var subQ4=sQuery(id+"F1.wireOp",EDGE,"E0");var subQ15=sQuery(id+"F1.wireOp",EDGE,"E5");Q0=makeQuery(id+"F6.boolean.opBoolean","SPLIT",FACE,{"disambiguationData":[TD([makeQuery(id+"F2.opExtrude","SWEPT_FACE",FACE,{"disambiguationData":[OSD([subQ4])]})])],"derivedFrom":makeQuery(id+"F6.opExtrude","SWEPT_FACE",FACE,{"disambiguationData":[OSD([subQ15,subQ0])]})});}
            var sketch = newSketch(context, id + "F10", { "sketchPlane" : qUnion([Q0])});
            skLineSegment(sketch, "E48", {"start": v(-50.23, 12.7) * mm, "end": v(-7.66, 50.8) * mm});
            skLineSegment(sketch, "E49", {"start": v(-7.66, 50.8) * mm, "end": v(-7.66, 52.64) * mm});
            skLineSegment(sketch, "E50", {"start": v(-7.66, 52.64) * mm, "end": v(-57.52, 52.64) * mm});
            skLineSegment(sketch, "E51", {"start": v(-57.52, 52.64) * mm, "end": v(-56.45, 14.01) * mm});
            skLineSegment(sketch, "E52", {"start": v(-56.45, 14.01) * mm, "end": v(-50.23, 12.7) * mm});
            skSolve(sketch);
        }
        {
            var Q0;
            Q0 = qSketchRegion(id + "F8", true);
            extrude(context, id + "F11", {"entities" : qUnion([Q0]), "operationType" : NewBodyOperationType.REMOVE, "oppositeDirection" : true, "depth" : 15.24 * mm});
        }
        {
            var Q0;
            Q0 = qSketchRegion(id + "F9", true);
            extrude(context, id + "F12", {"entities" : qUnion([Q0]), "operationType" : NewBodyOperationType.REMOVE, "oppositeDirection" : true, "depth" : 15.24 * mm});
        }
        {
            var Q0;
            Q0 = qSketchRegion(id + "F10", true);
            extrude(context, id + "F13", {"entities" : qUnion([Q0]), "operationType" : NewBodyOperationType.REMOVE, "oppositeDirection" : true, "depth" : 15.24 * mm});
        }
        {
            var Q0;
            {var subQ0=sQuery(id+"F1.wireOp",EDGE,"E17");var subQ1=sQuery(id+"F1.wireOp",EDGE,"E7");var subQ2=sQuery(id+"F1.wireOp",EDGE,"E6");var subQ3=sQuery(id+"F1.wireOp",EDGE,"E5");var subQ4=sQuery(id+"F1.wireOp",EDGE,"E4");var subQ5=sQuery(id+"F1.wireOp",EDGE,"E0");var subQ6=sQuery(id+"F1.wireOp",EDGE,"E14");var subQ7=sQuery(id+"F1.wireOp",EDGE,"E15.trimOffspring");var subQ8=sQuery(id+"F1.wireOp",EDGE,"E12");var subQ9=sQuery(id+"F1.wireOp",EDGE,"E11.trimOffspring");var subQ10=sQuery(id+"F1.wireOp",EDGE,"E1");var subQ11=sQuery(id+"F1.wireOp",EDGE,"E16.trimOffspring");var subQ12=sQuery(id+"F1.wireOp",EDGE,"E13");var subQ13=sQuery(id+"F1.wireOp",EDGE,"E10.trimOffspring");var subQ14=sQuery(id+"F1.wireOp",EDGE,"E2");Q0=makeQuery(id+"F6.boolean.opBoolean","SPLIT",FACE,{"disambiguationData":[TD([makeQuery(id+"F2.opExtrude","SWEPT_FACE",FACE,{"disambiguationData":[OSD([subQ5])]}),makeQuery(id+"F2.opExtrude","CAP_FACE",FACE,{"disambiguationData":[OSD([subQ5,subQ10,subQ9,subQ8,subQ7])],"isStart":false}),makeQuery(id+"F3.opExtrude","CAP_FACE",FACE,{"disambiguationData":[OSD([subQ10,subQ14,subQ13,subQ9,subQ8,subQ12,subQ7,subQ11])],"isStart":false}),makeQuery(id+"F3.opExtrude","SWEPT_FACE",FACE,{"disambiguationData":[OSD([subQ10,subQ9,subQ8,subQ7])]}),makeQuery(id+"F4.opExtrude","CAP_FACE",FACE,{"disambiguationData":[OSD([subQ14,subQ13,subQ12,subQ6,subQ11])],"isStart":false}),makeQuery(id+"F4.opExtrude","SWEPT_FACE",FACE,{"disambiguationData":[OSD([subQ14,subQ13,subQ12,subQ11])]}),makeQuery(id+"F5.opExtrude","CAP_FACE",FACE,{"disambiguationData":[OSD([sQuery(id+"F1.wireOp",EDGE,"E3"),subQ6])],"isStart":false}),makeQuery(id+"F5.opExtrude","SWEPT_FACE",FACE,{"disambiguationData":[OSD([subQ6])]}),makeQuery(id+"F6.opExtrude","SWEPT_FACE",FACE,{"disambiguationData":[OSD([subQ5]),TDD([makeQuery(id+"F1.imprint","IMPRINT",EDGE,{"disambiguationData":[TD([[makeQuery(id+"F1.imprint","INTERSECT",VERTEX,{"derivedFrom":[subQ5,subQ2]}),1.0]])],"derivedFrom":subQ5})])]}),makeQuery(id+"F6.opExtrude","CAP_FACE",FACE,{"disambiguationData":[OSD([subQ5,subQ4,subQ3,subQ2,subQ1,subQ0,sQuery(id+"F1.wireOp",EDGE,"E18")])],"isStart":false}),makeQuery(id+"F6.opExtrude","SWEPT_FACE",FACE,{"disambiguationData":[OSD([subQ5]),TDD([makeQuery(id+"F1.imprint","IMPRINT",EDGE,{"disambiguationData":[TD([[makeQuery(id+"F1.imprint","INTERSECT",VERTEX,{"derivedFrom":[subQ5,subQ4]}),-1.0]])],"derivedFrom":subQ5})])]})]),OD(1.0)],"derivedFrom":makeQuery(id+"F6.opExtrude","SWEPT_FACE",FACE,{"disambiguationData":[OSD([subQ4,subQ2,subQ0])]})});}
            var sketch = newSketch(context, id + "F14", { "sketchPlane" : qUnion([Q0])});
            skLineSegment(sketch, "E53", {"start": v(-50.23, 12.7) * mm, "end": v(-7.65, 50.8) * mm});
            skLineSegment(sketch, "E54", {"start": v(-7.65, 50.8) * mm, "end": v(-7.65, 52.59) * mm});
            skLineSegment(sketch, "E55", {"start": v(-7.65, 52.59) * mm, "end": v(-58.24, 53.24) * mm});
            skLineSegment(sketch, "E56", {"start": v(-58.24, 53.24) * mm, "end": v(-54.04, 12.7) * mm});
            skLineSegment(sketch, "E57", {"start": v(-54.04, 12.7) * mm, "end": v(-50.23, 12.7) * mm});
            skSolve(sketch);
        }
        {
            var Q0;
            Q0 = qSketchRegion(id + "F14", true);
            extrude(context, id + "F15", {"entities" : qUnion([Q0]), "operationType" : NewBodyOperationType.REMOVE, "oppositeDirection" : true, "depth" : 15.24 * mm});
        }
        {
            var Q0;
            Q0=qCreatedBy(id+"F0.planeOp",FACE);
            var sketch = newSketch(context, id + "F16", { "sketchPlane" : qUnion([Q0])});
            skLineSegment(sketch, "E58.bottom", {"start": v(6.28, -5.08) * mm, "end": v(47.69, -5.08) * mm});
            skLineSegment(sketch, "E58.top", {"start": v(6.28, 5.08) * mm, "end": v(47.69, 5.08) * mm});
            skLineSegment(sketch, "E58.left", {"start": v(6.28, -5.08) * mm, "end": v(6.28, 5.08) * mm});
            skLineSegment(sketch, "E58.right", {"start": v(47.69, -5.08) * mm, "end": v(47.69, 5.08) * mm});
            skLineSegment(sketch, "E59.bottom", {"start": v(-6.28, -5.08) * mm, "end": v(-47.69, -5.08) * mm});
            skLineSegment(sketch, "E59.top", {"start": v(-6.28, 5.08) * mm, "end": v(-47.69, 5.08) * mm});
            skLineSegment(sketch, "E59.left", {"start": v(-6.28, -5.08) * mm, "end": v(-6.28, 5.08) * mm});
            skLineSegment(sketch, "E59.right", {"start": v(-47.69, -5.08) * mm, "end": v(-47.69, 5.08) * mm});
            skLineSegment(sketch, "E60.bottom", {"start": v(-5.08, 6.28) * mm, "end": v(5.08, 6.28) * mm});
            skLineSegment(sketch, "E60.top", {"start": v(-5.08, 47.69) * mm, "end": v(5.08, 47.69) * mm});
            skLineSegment(sketch, "E60.left", {"start": v(-5.08, 6.28) * mm, "end": v(-5.08, 47.69) * mm});
            skLineSegment(sketch, "E60.right", {"start": v(5.08, 6.28) * mm, "end": v(5.08, 47.69) * mm});
            skLineSegment(sketch, "E61.bottom", {"start": v(-5.08, -6.28) * mm, "end": v(5.08, -6.28) * mm});
            skLineSegment(sketch, "E61.top", {"start": v(-5.08, -47.69) * mm, "end": v(5.08, -47.69) * mm});
            skLineSegment(sketch, "E61.left", {"start": v(-5.08, -6.28) * mm, "end": v(-5.08, -47.69) * mm});
            skLineSegment(sketch, "E61.right", {"start": v(5.08, -6.28) * mm, "end": v(5.08, -47.69) * mm});
            skSolve(sketch);
        }
        {
            var Q0;
            Q0 = qSketchRegion(id + "F16", true);
            extrude(context, id + "F17", {"entities" : qUnion([Q0]), "operationType" : NewBodyOperationType.REMOVE, "oppositeDirection" : true, "depth" : 44.45 * mm});
        }
        {
            var Q0;
            {var subQ0=sQuery(id+"F1.wireOp",EDGE,"E22");var subQ4=sQuery(id+"F1.wireOp",EDGE,"E3");var subQ5=makeQuery(id+"F1.imprint","INTERSECT",VERTEX,{"derivedFrom":[subQ4,subQ0]});Q0=makeQuery(id+"F1.imprint","IMPRINT",FACE,{"disambiguationData":[TD([[makeQuery(id+"F1.imprint","IMPRINT",EDGE,{"disambiguationData":[TD([[subQ5,-1.0]])],"derivedFrom":subQ4}),1.0]])]});}
            var Q1;
            {var subQ3=sQuery(id+"F1.wireOp",EDGE,"E3");var subQ5=sQuery(id+"F1.wireOp",EDGE,"E22");var subQ6=makeQuery(id+"F1.imprint","INTERSECT",VERTEX,{"derivedFrom":[subQ3,subQ5]});Q1=makeQuery(id+"F1.imprint","IMPRINT",FACE,{"disambiguationData":[TD([[makeQuery(id+"F1.imprint","IMPRINT",EDGE,{"disambiguationData":[TD([[subQ6,-1.0]])],"derivedFrom":subQ3}),-1.0]])]});}
            var Q2;
            {var subQ0=sQuery(id+"F1.wireOp",EDGE,"E22");var subQ1=sQuery(id+"F1.wireOp",EDGE,"E10.trimOffspring");var subQ2=makeQuery(id+"F1.imprint","INTERSECT",VERTEX,{"derivedFrom":[subQ1,subQ0]});Q2=makeQuery(id+"F1.imprint","IMPRINT",FACE,{"disambiguationData":[TD([[makeQuery(id+"F1.imprint","IMPRINT",EDGE,{"disambiguationData":[TD([[subQ2,-1.0]])],"derivedFrom":subQ1}),1.0]])]});}
            var Q3;
            {var subQ0=sQuery(id+"F1.wireOp",EDGE,"E22");var subQ1=sQuery(id+"F1.wireOp",EDGE,"E10.trimOffspring");var subQ2=makeQuery(id+"F1.imprint","INTERSECT",VERTEX,{"derivedFrom":[subQ1,subQ0]});Q3=makeQuery(id+"F1.imprint","IMPRINT",FACE,{"disambiguationData":[TD([[makeQuery(id+"F1.imprint","IMPRINT",EDGE,{"disambiguationData":[TD([[subQ2,-1.0]])],"derivedFrom":subQ1}),-1.0]])]});}
            var Q4;
            {var subQ0=sQuery(id+"F1.wireOp",EDGE,"E22");var subQ1=sQuery(id+"F1.wireOp",EDGE,"E0");var subQ2=makeQuery(id+"F1.imprint","INTERSECT",VERTEX,{"derivedFrom":[subQ1,subQ0]});Q4=makeQuery(id+"F1.imprint","IMPRINT",FACE,{"disambiguationData":[TD([[makeQuery(id+"F1.imprint","IMPRINT",EDGE,{"disambiguationData":[TD([[subQ2,-1.0]])],"derivedFrom":subQ1}),1.0]])]});}
            var Q5;
            {var subQ0=sQuery(id+"F1.wireOp",EDGE,"E17");var subQ3=sQuery(id+"F1.wireOp",EDGE,"E27");var subQ5=makeQuery(id+"F1.imprint","INTERSECT",VERTEX,{"derivedFrom":[subQ0,subQ3]});Q5=makeQuery(id+"F1.imprint","IMPRINT",FACE,{"disambiguationData":[TD([[makeQuery(id+"F1.imprint","IMPRINT",EDGE,{"disambiguationData":[TD([[subQ5,-1.0]])],"derivedFrom":subQ3}),1.0]])]});}
            var Q6;
            {var subQ0=sQuery(id+"F1.wireOp",EDGE,"E14");var subQ1=sQuery(id+"F1.wireOp",EDGE,"E4");var subQ2=makeQuery(id+"F1.imprint","INTERSECT",VERTEX,{"derivedFrom":[subQ1,subQ0]});Q6=makeQuery(id+"F1.imprint","IMPRINT",FACE,{"disambiguationData":[TD([[makeQuery(id+"F1.imprint","IMPRINT",EDGE,{"disambiguationData":[TD([[subQ2,1.0]])],"derivedFrom":subQ0}),1.0]])]});}
            var Q7;
            {var subQ1=sQuery(id+"F1.wireOp",EDGE,"E4");var subQ7=sQuery(id+"F1.wireOp",EDGE,"E31");var subQ9=makeQuery(id+"F1.imprint","INTERSECT",VERTEX,{"derivedFrom":[subQ1,subQ7]});Q7=makeQuery(id+"F1.imprint","IMPRINT",FACE,{"disambiguationData":[TD([[makeQuery(id+"F1.imprint","IMPRINT",EDGE,{"disambiguationData":[TD([[subQ9,1.0]])],"derivedFrom":subQ1}),-1.0]])]});}
            var Q8;
            {var subQ0=sQuery(id+"F1.wireOp",EDGE,"E28");var subQ1=sQuery(id+"F1.wireOp",EDGE,"E10.trimOffspring");var subQ2=makeQuery(id+"F1.imprint","INTERSECT",VERTEX,{"derivedFrom":[subQ1,subQ0]});Q8=makeQuery(id+"F1.imprint","IMPRINT",FACE,{"disambiguationData":[TD([[makeQuery(id+"F1.imprint","IMPRINT",EDGE,{"disambiguationData":[TD([[subQ2,-1.0]])],"derivedFrom":subQ1}),-1.0]])]});}
            var Q9;
            {var subQ0=sQuery(id+"F1.wireOp",EDGE,"E28");var subQ1=sQuery(id+"F1.wireOp",EDGE,"E0");var subQ2=makeQuery(id+"F1.imprint","INTERSECT",VERTEX,{"derivedFrom":[subQ1,subQ0]});Q9=makeQuery(id+"F1.imprint","IMPRINT",FACE,{"disambiguationData":[TD([[makeQuery(id+"F1.imprint","IMPRINT",EDGE,{"disambiguationData":[TD([[subQ2,-1.0]])],"derivedFrom":subQ1}),1.0]])]});}
            var Q10;
            {var subQ0=sQuery(id+"F1.wireOp",EDGE,"E32");var subQ1=sQuery(id+"F1.wireOp",EDGE,"E0");var subQ2=makeQuery(id+"F1.imprint","INTERSECT",VERTEX,{"derivedFrom":[subQ1,subQ0]});Q10=makeQuery(id+"F1.imprint","IMPRINT",FACE,{"disambiguationData":[TD([[makeQuery(id+"F1.imprint","IMPRINT",EDGE,{"disambiguationData":[TD([[subQ2,1.0]])],"derivedFrom":subQ1}),1.0]])]});}
            var Q11;
            {var subQ0=sQuery(id+"F1.wireOp",EDGE,"E19");var subQ1=sQuery(id+"F1.wireOp",EDGE,"E0");var subQ2=makeQuery(id+"F1.imprint","INTERSECT",VERTEX,{"derivedFrom":[subQ1,subQ0]});Q11=makeQuery(id+"F1.imprint","IMPRINT",FACE,{"disambiguationData":[TD([[makeQuery(id+"F1.imprint","IMPRINT",EDGE,{"disambiguationData":[TD([[subQ2,1.0]])],"derivedFrom":subQ1}),1.0]])]});}
            var Q12;
            {var subQ0=sQuery(id+"F1.wireOp",EDGE,"E33");var subQ1=sQuery(id+"F1.wireOp",EDGE,"E10.trimOffspring");var subQ2=makeQuery(id+"F1.imprint","INTERSECT",VERTEX,{"derivedFrom":[subQ1,subQ0]});Q12=makeQuery(id+"F1.imprint","IMPRINT",FACE,{"disambiguationData":[TD([[makeQuery(id+"F1.imprint","IMPRINT",EDGE,{"disambiguationData":[TD([[subQ2,-1.0]])],"derivedFrom":subQ1}),-1.0]])]});}
            var Q13;
            {var subQ0=sQuery(id+"F1.wireOp",EDGE,"E32");var subQ1=sQuery(id+"F1.wireOp",EDGE,"E10.trimOffspring");var subQ2=makeQuery(id+"F1.imprint","INTERSECT",VERTEX,{"derivedFrom":[subQ1,subQ0]});Q13=makeQuery(id+"F1.imprint","IMPRINT",FACE,{"disambiguationData":[TD([[makeQuery(id+"F1.imprint","IMPRINT",EDGE,{"disambiguationData":[TD([[subQ2,-1.0]])],"derivedFrom":subQ1}),-1.0]])]});}
            var Q14;
            {var subQ5=sQuery(id+"F1.wireOp",EDGE,"E6");var subQ7=sQuery(id+"F1.wireOp",EDGE,"E33");var subQ9=makeQuery(id+"F1.imprint","INTERSECT",VERTEX,{"derivedFrom":[subQ5,subQ7]});Q14=makeQuery(id+"F1.imprint","IMPRINT",FACE,{"disambiguationData":[TD([[makeQuery(id+"F1.imprint","IMPRINT",EDGE,{"disambiguationData":[TD([[subQ9,1.0]])],"derivedFrom":subQ5}),1.0]])]});}
            var Q15;
            {var subQ0=sQuery(id+"F1.wireOp",EDGE,"E32");var subQ1=sQuery(id+"F1.wireOp",EDGE,"E10.trimOffspring");var subQ2=makeQuery(id+"F1.imprint","INTERSECT",VERTEX,{"derivedFrom":[subQ1,subQ0]});Q15=makeQuery(id+"F1.imprint","IMPRINT",FACE,{"disambiguationData":[TD([[makeQuery(id+"F1.imprint","IMPRINT",EDGE,{"disambiguationData":[TD([[subQ2,-1.0]])],"derivedFrom":subQ1}),1.0]])]});}
            var Q16;
            {var subQ0=sQuery(id+"F1.wireOp",EDGE,"E6");var subQ5=sQuery(id+"F1.wireOp",EDGE,"E14");var subQ6=makeQuery(id+"F1.imprint","INTERSECT",VERTEX,{"derivedFrom":[subQ0,subQ5]});Q16=makeQuery(id+"F1.imprint","IMPRINT",FACE,{"disambiguationData":[TD([[makeQuery(id+"F1.imprint","IMPRINT",EDGE,{"disambiguationData":[TD([[subQ6,-1.0]])],"derivedFrom":subQ5}),1.0]])]});}
            var Q17;
            {var subQ0=sQuery(id+"F1.wireOp",EDGE,"E32");var subQ1=sQuery(id+"F1.wireOp",EDGE,"E3");var subQ2=makeQuery(id+"F1.imprint","INTERSECT",VERTEX,{"derivedFrom":[subQ1,subQ0]});Q17=makeQuery(id+"F1.imprint","IMPRINT",FACE,{"disambiguationData":[TD([[makeQuery(id+"F1.imprint","IMPRINT",EDGE,{"disambiguationData":[TD([[subQ2,-1.0]])],"derivedFrom":subQ1}),-1.0]])]});}
            var Q18;
            {var subQ5=sQuery(id+"F1.wireOp",EDGE,"E32");var subQ7=sQuery(id+"F1.wireOp",EDGE,"E3");var subQ8=makeQuery(id+"F1.imprint","INTERSECT",VERTEX,{"derivedFrom":[subQ7,subQ5]});Q18=makeQuery(id+"F1.imprint","IMPRINT",FACE,{"disambiguationData":[TD([[makeQuery(id+"F1.imprint","IMPRINT",EDGE,{"disambiguationData":[TD([[subQ8,-1.0]])],"derivedFrom":subQ7}),1.0]])]});}
            var Q19;
            {var subQ0=sQuery(id+"F1.wireOp",EDGE,"E17");var subQ3=sQuery(id+"F1.wireOp",EDGE,"E32");var subQ5=makeQuery(id+"F1.imprint","INTERSECT",VERTEX,{"derivedFrom":[subQ0,subQ3]});Q19=makeQuery(id+"F1.imprint","IMPRINT",FACE,{"disambiguationData":[TD([[makeQuery(id+"F1.imprint","IMPRINT",EDGE,{"disambiguationData":[TD([[subQ5,-1.0]])],"derivedFrom":subQ3}),-1.0]])]});}
            var Q20;
            {var subQ0=sQuery(id+"F1.wireOp",EDGE,"E18");var subQ3=sQuery(id+"F1.wireOp",EDGE,"E36");var subQ5=makeQuery(id+"F1.imprint","INTERSECT",VERTEX,{"derivedFrom":[subQ0,subQ3]});Q20=makeQuery(id+"F1.imprint","IMPRINT",FACE,{"disambiguationData":[TD([[makeQuery(id+"F1.imprint","IMPRINT",EDGE,{"disambiguationData":[TD([[subQ5,-1.0]])],"derivedFrom":subQ3}),-1.0]])]});}
            var Q21;
            {var subQ0=sQuery(id+"F1.wireOp",EDGE,"E5");var subQ5=sQuery(id+"F1.wireOp",EDGE,"E14");var subQ6=makeQuery(id+"F1.imprint","INTERSECT",VERTEX,{"derivedFrom":[subQ0,subQ5]});Q21=makeQuery(id+"F1.imprint","IMPRINT",FACE,{"disambiguationData":[TD([[makeQuery(id+"F1.imprint","IMPRINT",EDGE,{"disambiguationData":[TD([[subQ6,-1.0]])],"derivedFrom":subQ5}),1.0]])]});}
            var Q22;
            {var subQ0=sQuery(id+"F1.wireOp",EDGE,"E37");var subQ1=sQuery(id+"F1.wireOp",EDGE,"E1");var subQ2=makeQuery(id+"F1.imprint","INTERSECT",VERTEX,{"derivedFrom":[subQ1,subQ0]});Q22=makeQuery(id+"F1.imprint","IMPRINT",FACE,{"disambiguationData":[TD([[makeQuery(id+"F1.imprint","IMPRINT",EDGE,{"disambiguationData":[TD([[subQ2,-1.0]])],"derivedFrom":subQ1}),1.0]])]});}
            var Q23;
            {var subQ1=sQuery(id+"F1.wireOp",EDGE,"E2");var subQ7=sQuery(id+"F1.wireOp",EDGE,"E37");var subQ9=makeQuery(id+"F1.imprint","INTERSECT",VERTEX,{"derivedFrom":[subQ1,subQ7]});Q23=makeQuery(id+"F1.imprint","IMPRINT",FACE,{"disambiguationData":[TD([[makeQuery(id+"F1.imprint","IMPRINT",EDGE,{"disambiguationData":[TD([[subQ9,-1.0]])],"derivedFrom":subQ1}),1.0]])]});}
            var Q24;
            {var subQ0=sQuery(id+"F1.wireOp",EDGE,"E36");var subQ1=sQuery(id+"F1.wireOp",EDGE,"E0");var subQ2=makeQuery(id+"F1.imprint","INTERSECT",VERTEX,{"derivedFrom":[subQ1,subQ0]});Q24=makeQuery(id+"F1.imprint","IMPRINT",FACE,{"disambiguationData":[TD([[makeQuery(id+"F1.imprint","IMPRINT",EDGE,{"disambiguationData":[TD([[subQ2,1.0]])],"derivedFrom":subQ1}),1.0]])]});}
            var Q25;
            {var subQ5=sQuery(id+"F1.wireOp",EDGE,"E36");var subQ7=sQuery(id+"F1.wireOp",EDGE,"E3");var subQ9=makeQuery(id+"F1.imprint","INTERSECT",VERTEX,{"derivedFrom":[subQ7,subQ5]});Q25=makeQuery(id+"F1.imprint","IMPRINT",FACE,{"disambiguationData":[TD([[makeQuery(id+"F1.imprint","IMPRINT",EDGE,{"disambiguationData":[TD([[subQ9,-1.0]])],"derivedFrom":subQ7}),1.0]])]});}
            var Q26;
            {var subQ0=sQuery(id+"F1.wireOp",EDGE,"E36");var subQ1=sQuery(id+"F1.wireOp",EDGE,"E3");var subQ2=makeQuery(id+"F1.imprint","INTERSECT",VERTEX,{"derivedFrom":[subQ1,subQ0]});Q26=makeQuery(id+"F1.imprint","IMPRINT",FACE,{"disambiguationData":[TD([[makeQuery(id+"F1.imprint","IMPRINT",EDGE,{"disambiguationData":[TD([[subQ2,-1.0]])],"derivedFrom":subQ1}),-1.0]])]});}
            var Q27;
            {var subQ0=sQuery(id+"F1.wireOp",EDGE,"E36");var subQ1=sQuery(id+"F1.wireOp",EDGE,"E2");var subQ2=makeQuery(id+"F1.imprint","INTERSECT",VERTEX,{"derivedFrom":[subQ1,subQ0]});Q27=makeQuery(id+"F1.imprint","IMPRINT",FACE,{"disambiguationData":[TD([[makeQuery(id+"F1.imprint","IMPRINT",EDGE,{"disambiguationData":[TD([[subQ2,-1.0]])],"derivedFrom":subQ1}),1.0]])]});}
            var Q28;
            {var subQ0=sQuery(id+"F1.wireOp",EDGE,"E36");var subQ1=sQuery(id+"F1.wireOp",EDGE,"E1");var subQ2=makeQuery(id+"F1.imprint","INTERSECT",VERTEX,{"derivedFrom":[subQ1,subQ0]});Q28=makeQuery(id+"F1.imprint","IMPRINT",FACE,{"disambiguationData":[TD([[makeQuery(id+"F1.imprint","IMPRINT",EDGE,{"disambiguationData":[TD([[subQ2,-1.0]])],"derivedFrom":subQ1}),1.0]])]});}
            var Q29;
            {var subQ0=sQuery(id+"F1.wireOp",EDGE,"E21");var subQ1=sQuery(id+"F1.wireOp",EDGE,"E0");var subQ2=makeQuery(id+"F1.imprint","INTERSECT",VERTEX,{"derivedFrom":[subQ1,subQ0]});Q29=makeQuery(id+"F1.imprint","IMPRINT",FACE,{"disambiguationData":[TD([[makeQuery(id+"F1.imprint","IMPRINT",EDGE,{"disambiguationData":[TD([[subQ2,1.0]])],"derivedFrom":subQ1}),1.0]])]});}
            var Q30;
            {var subQ5=sQuery(id+"F1.wireOp",EDGE,"E35");var subQ7=sQuery(id+"F1.wireOp",EDGE,"E3");var subQ8=makeQuery(id+"F1.imprint","INTERSECT",VERTEX,{"derivedFrom":[subQ7,subQ5]});Q30=makeQuery(id+"F1.imprint","IMPRINT",FACE,{"disambiguationData":[TD([[makeQuery(id+"F1.imprint","IMPRINT",EDGE,{"disambiguationData":[TD([[subQ8,1.0]])],"derivedFrom":subQ7}),1.0]])]});}
            var Q31;
            {var subQ0=sQuery(id+"F1.wireOp",EDGE,"E35");var subQ1=sQuery(id+"F1.wireOp",EDGE,"E3");var subQ2=makeQuery(id+"F1.imprint","INTERSECT",VERTEX,{"derivedFrom":[subQ1,subQ0]});Q31=makeQuery(id+"F1.imprint","IMPRINT",FACE,{"disambiguationData":[TD([[makeQuery(id+"F1.imprint","IMPRINT",EDGE,{"disambiguationData":[TD([[subQ2,1.0]])],"derivedFrom":subQ1}),-1.0]])]});}
            var Q32;
            {var subQ0=sQuery(id+"F1.wireOp",EDGE,"E20");var subQ1=sQuery(id+"F1.wireOp",EDGE,"E2");var subQ2=makeQuery(id+"F1.imprint","INTERSECT",VERTEX,{"derivedFrom":[subQ1,subQ0]});Q32=makeQuery(id+"F1.imprint","IMPRINT",FACE,{"disambiguationData":[TD([[makeQuery(id+"F1.imprint","IMPRINT",EDGE,{"disambiguationData":[TD([[subQ2,-1.0]])],"derivedFrom":subQ1}),1.0]])]});}
            var Q33;
            {var subQ0=sQuery(id+"F1.wireOp",EDGE,"E20");var subQ1=sQuery(id+"F1.wireOp",EDGE,"E1");var subQ2=makeQuery(id+"F1.imprint","INTERSECT",VERTEX,{"derivedFrom":[subQ1,subQ0]});Q33=makeQuery(id+"F1.imprint","IMPRINT",FACE,{"disambiguationData":[TD([[makeQuery(id+"F1.imprint","IMPRINT",EDGE,{"disambiguationData":[TD([[subQ2,-1.0]])],"derivedFrom":subQ1}),1.0]])]});}
            var Q34;
            {var subQ0=sQuery(id+"F1.wireOp",EDGE,"E20");var subQ1=sQuery(id+"F1.wireOp",EDGE,"E0");var subQ2=makeQuery(id+"F1.imprint","INTERSECT",VERTEX,{"derivedFrom":[subQ1,subQ0]});Q34=makeQuery(id+"F1.imprint","IMPRINT",FACE,{"disambiguationData":[TD([[makeQuery(id+"F1.imprint","IMPRINT",EDGE,{"disambiguationData":[TD([[subQ2,-1.0]])],"derivedFrom":subQ1}),1.0]])]});}
            var Q35;
            {var subQ0=sQuery(id+"F1.wireOp",EDGE,"E34");var subQ1=sQuery(id+"F1.wireOp",EDGE,"E0");var subQ2=makeQuery(id+"F1.imprint","INTERSECT",VERTEX,{"derivedFrom":[subQ1,subQ0]});Q35=makeQuery(id+"F1.imprint","IMPRINT",FACE,{"disambiguationData":[TD([[makeQuery(id+"F1.imprint","IMPRINT",EDGE,{"disambiguationData":[TD([[subQ2,1.0]])],"derivedFrom":subQ1}),1.0]])]});}
            var Q36;
            {var subQ0=sQuery(id+"F1.wireOp",EDGE,"E35");var subQ1=sQuery(id+"F1.wireOp",EDGE,"E1");var subQ2=makeQuery(id+"F1.imprint","INTERSECT",VERTEX,{"derivedFrom":[subQ1,subQ0]});Q36=makeQuery(id+"F1.imprint","IMPRINT",FACE,{"disambiguationData":[TD([[makeQuery(id+"F1.imprint","IMPRINT",EDGE,{"disambiguationData":[TD([[subQ2,-1.0]])],"derivedFrom":subQ1}),1.0]])]});}
            var Q37;
            {var subQ3=sQuery(id+"F1.wireOp",EDGE,"E2");var subQ5=sQuery(id+"F1.wireOp",EDGE,"E35");var subQ6=makeQuery(id+"F1.imprint","INTERSECT",VERTEX,{"derivedFrom":[subQ3,subQ5]});Q37=makeQuery(id+"F1.imprint","IMPRINT",FACE,{"disambiguationData":[TD([[makeQuery(id+"F1.imprint","IMPRINT",EDGE,{"disambiguationData":[TD([[subQ6,-1.0]])],"derivedFrom":subQ3}),1.0]])]});}
            var Q38;
            {var subQ0=sQuery(id+"F1.wireOp",EDGE,"E7");var subQ5=sQuery(id+"F1.wireOp",EDGE,"E14");var subQ7=makeQuery(id+"F1.imprint","INTERSECT",VERTEX,{"derivedFrom":[subQ0,subQ5]});Q38=makeQuery(id+"F1.imprint","IMPRINT",FACE,{"disambiguationData":[TD([[makeQuery(id+"F1.imprint","IMPRINT",EDGE,{"disambiguationData":[TD([[subQ7,1.0]])],"derivedFrom":subQ5}),1.0]])]});}
            var Q39;
            {var subQ0=sQuery(id+"F1.wireOp",EDGE,"E18");var subQ3=sQuery(id+"F1.wireOp",EDGE,"E35");var subQ5=makeQuery(id+"F1.imprint","INTERSECT",VERTEX,{"derivedFrom":[subQ0,subQ3]});Q39=makeQuery(id+"F1.imprint","IMPRINT",FACE,{"disambiguationData":[TD([[makeQuery(id+"F1.imprint","IMPRINT",EDGE,{"disambiguationData":[TD([[subQ5,-1.0]])],"derivedFrom":subQ3}),1.0]])]});}
            extrude(context, id + "F18", {"entities" : qUnion([Q0, Q1, Q2, Q3, Q4, Q5, Q6, Q7, Q8, Q9, Q10, Q11, Q12, Q13, Q14, Q15, Q16, Q17, Q18, Q19, Q20, Q21, Q22, Q23, Q24, Q25, Q26, Q27, Q28, Q29, Q30, Q31, Q32, Q33, Q34, Q35, Q36, Q37, Q38, Q39]), "operationType" : NewBodyOperationType.ADD, "depth" : 50.8 * mm});
        }
        {
            var Q0;
            Q0=qCreatedBy(id+"F0.planeOp",FACE);
            var sketch = newSketch(context, id + "F19", { "sketchPlane" : qUnion([Q0])});
            skLineSegment(sketch, "E62", {"start": v(-10.16, -10.16) * mm, "end": v(-10.16, -17.32) * mm});
            skLineSegment(sketch, "E63", {"start": v(-10.16, -10.16) * mm, "end": v(-39.17, -10.16) * mm});
            skLineSegment(sketch, "E64", {"start": v(-39.17, -10.16) * mm, "end": v(-39.17, -17.32) * mm});
            skLineSegment(sketch, "E65", {"start": v(-39.17, -17.32) * mm, "end": v(-10.16, -17.32) * mm});
            skLineSegment(sketch, "E66", {"start": v(-10.16, -19.86) * mm, "end": v(-10.16, -27.03) * mm});
            skLineSegment(sketch, "E67", {"start": v(-10.16, -19.86) * mm, "end": v(-39.17, -19.86) * mm});
            skLineSegment(sketch, "E68", {"start": v(-39.17, -19.86) * mm, "end": v(-39.17, -27.03) * mm});
            skLineSegment(sketch, "E69", {"start": v(-39.17, -27.03) * mm, "end": v(-10.16, -27.03) * mm});
            skLineSegment(sketch, "E70", {"start": v(-10.16, 10.16) * mm, "end": v(-39.17, 10.16) * mm});
            skLineSegment(sketch, "E71", {"start": v(-39.17, 10.16) * mm, "end": v(-39.17, 17.32) * mm});
            skLineSegment(sketch, "E72", {"start": v(-39.17, 17.32) * mm, "end": v(-10.16, 17.32) * mm});
            skLineSegment(sketch, "E73", {"start": v(-10.16, 17.32) * mm, "end": v(-10.16, 10.16) * mm});
            skLineSegment(sketch, "E74", {"start": v(-10.16, 19.86) * mm, "end": v(-10.16, 27.03) * mm});
            skLineSegment(sketch, "E75", {"start": v(-10.16, 27.03) * mm, "end": v(-39.17, 27.03) * mm});
            skLineSegment(sketch, "E76", {"start": v(-39.17, 27.03) * mm, "end": v(-39.17, 19.86) * mm});
            skLineSegment(sketch, "E77", {"start": v(-39.17, 19.86) * mm, "end": v(-10.16, 19.86) * mm});
            skLineSegment(sketch, "E78", {"start": v(10.16, 27.03) * mm, "end": v(39.17, 27.03) * mm});
            skLineSegment(sketch, "E79", {"start": v(39.17, 27.03) * mm, "end": v(39.17, 19.86) * mm});
            skLineSegment(sketch, "E80", {"start": v(39.17, 19.86) * mm, "end": v(10.16, 19.86) * mm});
            skLineSegment(sketch, "E81", {"start": v(10.16, 19.86) * mm, "end": v(10.16, 27.03) * mm});
            skLineSegment(sketch, "E82", {"start": v(10.16, 17.32) * mm, "end": v(39.17, 17.32) * mm});
            skLineSegment(sketch, "E83", {"start": v(39.17, 17.32) * mm, "end": v(39.17, 10.16) * mm});
            skLineSegment(sketch, "E84", {"start": v(39.17, 10.16) * mm, "end": v(10.16, 10.16) * mm});
            skLineSegment(sketch, "E85", {"start": v(10.16, 10.16) * mm, "end": v(10.16, 17.32) * mm});
            skLineSegment(sketch, "E86", {"start": v(10.16, -10.16) * mm, "end": v(39.17, -10.16) * mm});
            skLineSegment(sketch, "E87", {"start": v(39.17, -10.16) * mm, "end": v(39.17, -17.32) * mm});
            skLineSegment(sketch, "E88", {"start": v(39.17, -17.32) * mm, "end": v(10.16, -17.32) * mm});
            skLineSegment(sketch, "E89", {"start": v(10.16, -17.32) * mm, "end": v(10.16, -10.16) * mm});
            skLineSegment(sketch, "E90", {"start": v(10.16, -19.86) * mm, "end": v(39.17, -19.86) * mm});
            skLineSegment(sketch, "E91", {"start": v(39.17, -19.86) * mm, "end": v(39.17, -27.03) * mm});
            skLineSegment(sketch, "E92", {"start": v(39.17, -27.03) * mm, "end": v(10.16, -27.03) * mm});
            skLineSegment(sketch, "E93", {"start": v(10.16, -27.03) * mm, "end": v(10.16, -19.86) * mm});
            skSolve(sketch);
        }
        {
            var Q0;
            Q0=makeQuery(id+"F18.opExtrude","SWEPT_FACE",FACE,{"disambiguationData":[OSD([sQuery(id+"F1.wireOp",EDGE,"E31")])]});
            var sketch = newSketch(context, id + "F20", { "sketchPlane" : qUnion([Q0])});
            skLineSegment(sketch, "E94", {"start": v(-7.62, 50.8) * mm, "end": v(-39.37, 12.7) * mm});
            skLineSegment(sketch, "E95", {"start": v(-39.37, 12.7) * mm, "end": v(-60.1, 12.7) * mm});
            skLineSegment(sketch, "E96", {"start": v(-60.1, 12.7) * mm, "end": v(-60.1, 65.61) * mm});
            skLineSegment(sketch, "E97", {"start": v(-60.1, 65.61) * mm, "end": v(-7.62, 65.61) * mm});
            skLineSegment(sketch, "E98", {"start": v(-7.62, 65.61) * mm, "end": v(-7.62, 50.8) * mm});
            skSolve(sketch);
        }
        {
            var Q0;
            Q0 = qSketchRegion(id + "F20", true);
            extrude(context, id + "F21", {"entities" : qUnion([Q0]), "operationType" : NewBodyOperationType.REMOVE, "oppositeDirection" : true, "depth" : 24.49 * mm});
        }
        {
            var Q0;
            Q0 = qSketchRegion(id + "F19", true);
            extrude(context, id + "F22", {"entities" : qUnion([Q0]), "operationType" : NewBodyOperationType.REMOVE, "oppositeDirection" : true, "depth" : 44.45 * mm});
        }
        {
            var Q0;
            Q0=makeQuery(id+"F18.opExtrude","SWEPT_FACE",FACE,{"disambiguationData":[OSD([sQuery(id+"F1.wireOp",EDGE,"E33")])]});
            var sketch = newSketch(context, id + "F23", { "sketchPlane" : qUnion([Q0])});
            skLineSegment(sketch, "E99", {"start": v(7.62, 50.8) * mm, "end": v(39.37, 12.7) * mm});
            skLineSegment(sketch, "E100", {"start": v(39.37, 12.7) * mm, "end": v(63.4, 12.7) * mm});
            skLineSegment(sketch, "E101", {"start": v(63.4, 12.7) * mm, "end": v(63.4, 58.95) * mm});
            skLineSegment(sketch, "E102", {"start": v(63.4, 58.95) * mm, "end": v(7.62, 58.95) * mm});
            skLineSegment(sketch, "E103", {"start": v(7.62, 58.95) * mm, "end": v(7.62, 50.8) * mm});
            skSolve(sketch);
        }
        {
            var Q0;
            Q0 = qSketchRegion(id + "F23", true);
            extrude(context, id + "F24", {"entities" : qUnion([Q0]), "operationType" : NewBodyOperationType.REMOVE, "oppositeDirection" : true, "depth" : 24.49 * mm});
        }
        {
            var Q0;
            Q0=makeQuery(id+"F18.opExtrude","SWEPT_FACE",FACE,{"disambiguationData":[OSD([sQuery(id+"F1.wireOp",EDGE,"E34")])]});
            var sketch = newSketch(context, id + "F25", { "sketchPlane" : qUnion([Q0])});
            skLineSegment(sketch, "E104", {"start": v(-7.62, 50.8) * mm, "end": v(-39.37, 12.7) * mm});
            skLineSegment(sketch, "E105", {"start": v(-39.37, 12.7) * mm, "end": v(-64.42, 12.7) * mm});
            skLineSegment(sketch, "E106", {"start": v(-64.42, 12.7) * mm, "end": v(-64.42, 60.83) * mm});
            skLineSegment(sketch, "E107", {"start": v(-64.42, 60.83) * mm, "end": v(-7.62, 60.83) * mm});
            skLineSegment(sketch, "E108", {"start": v(-7.62, 60.83) * mm, "end": v(-7.62, 50.8) * mm});
            skSolve(sketch);
        }
        {
            var Q0;
            Q0 = qSketchRegion(id + "F25", true);
            extrude(context, id + "F26", {"entities" : qUnion([Q0]), "operationType" : NewBodyOperationType.REMOVE, "oppositeDirection" : true, "depth" : 24.49 * mm});
        }
        {
            var Q0;
            Q0=makeQuery(id+"F18.opExtrude","SWEPT_FACE",FACE,{"disambiguationData":[OSD([sQuery(id+"F1.wireOp",EDGE,"E37")])]});
            var sketch = newSketch(context, id + "F27", { "sketchPlane" : qUnion([Q0])});
            skLineSegment(sketch, "E109", {"start": v(7.62, 50.8) * mm, "end": v(39.37, 12.7) * mm});
            skLineSegment(sketch, "E110", {"start": v(39.37, 12.7) * mm, "end": v(79.1, 12.7) * mm});
            skLineSegment(sketch, "E111", {"start": v(79.1, 12.7) * mm, "end": v(79.1, 63.6) * mm});
            skLineSegment(sketch, "E112", {"start": v(79.1, 63.6) * mm, "end": v(7.62, 58.32) * mm});
            skLineSegment(sketch, "E113", {"start": v(7.62, 58.32) * mm, "end": v(7.62, 50.8) * mm});
            skSolve(sketch);
        }
        {
            var Q0;
            Q0 = qSketchRegion(id + "F27", true);
            extrude(context, id + "F28", {"entities" : qUnion([Q0]), "operationType" : NewBodyOperationType.REMOVE, "oppositeDirection" : true, "depth" : 24.49 * mm});
        }
    });
